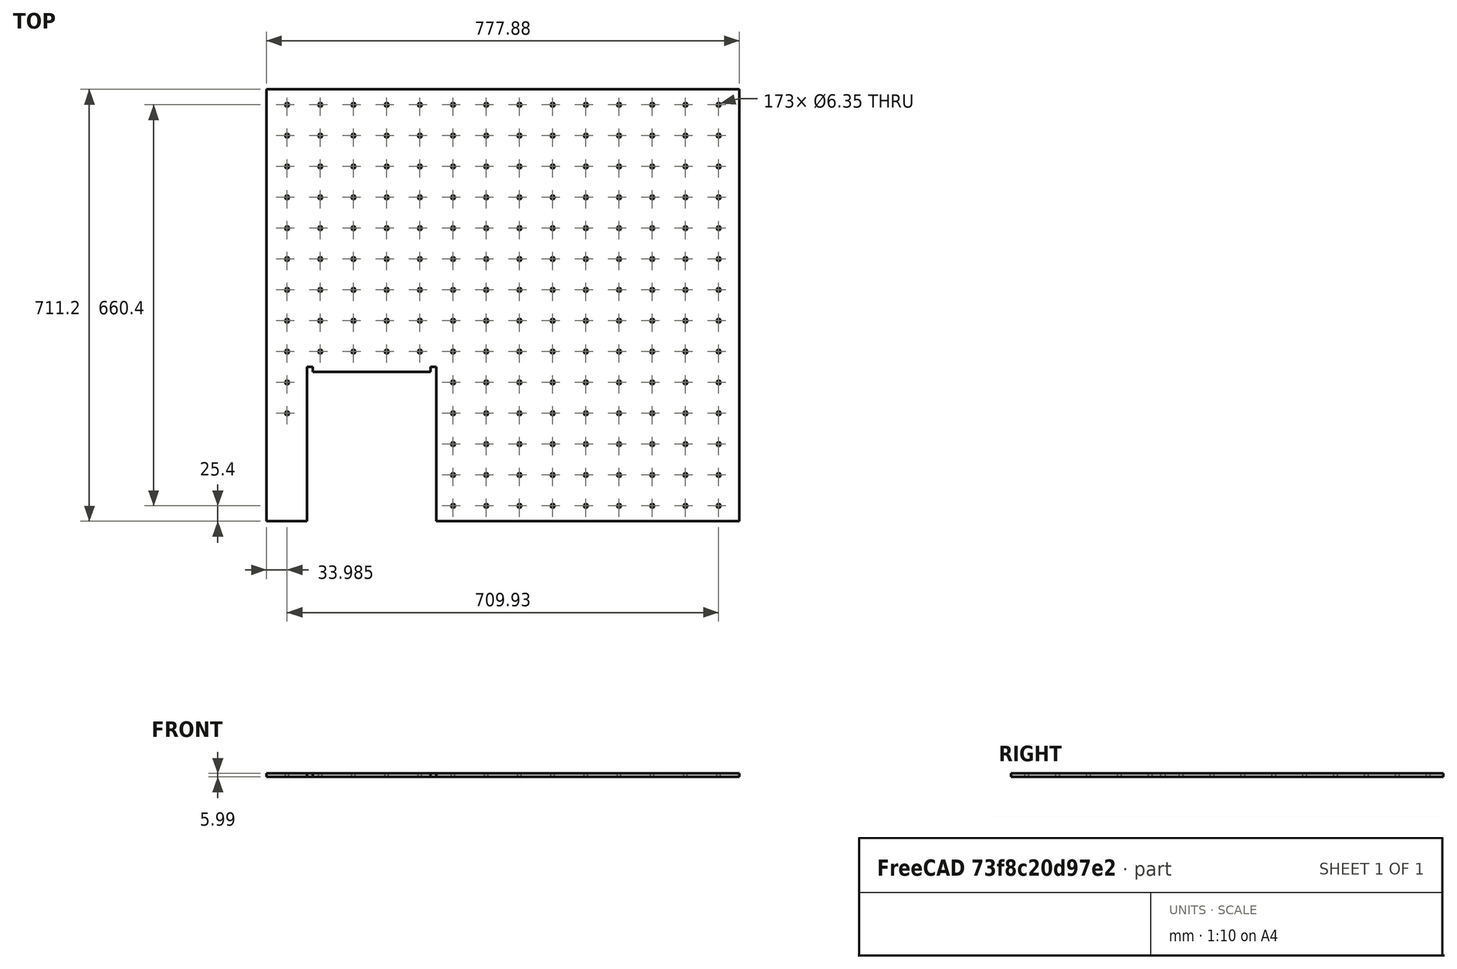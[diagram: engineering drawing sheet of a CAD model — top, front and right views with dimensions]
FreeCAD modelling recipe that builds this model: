
FCSTD DOCUMENT  (FreeCAD 0.19R24267 (Git))
Label: Inv1-P8
License: All rights reserved
LicenseURL: http://en.wikipedia.org/wiki/All_rights_reserved
objects: TechDraw::DrawViewDimension×15, TechDraw::DrawViewAnnotation×3, TechDraw::DrawProjGroupItem×2, TechDraw::DrawHatch×2, Sketcher::SketchObject×1, Part::Extrusion×1, TechDraw::DrawSVGTemplate×1, TechDraw::DrawProjGroup×1, TechDraw::DrawPage×1
note: 2 computed .brp shape members not serialized (recipe doc carries the construction recipe); baked Part::Feature solids carry a one-line shape summary decoded from their .brp

FEATURE [Sketcher::SketchObject] Sketch
  FullyConstrained = false
  sketch-geometry (352):
    g0: LineSegment StartX=0 StartY=0 StartZ=0 EndX=777.875 EndY=0 EndZ=0
    g1: LineSegment StartX=777.875 StartY=0 StartZ=0 EndX=777.875 EndY=-711.2 EndZ=0
    g2: LineSegment StartX=0 StartY=-711.2 StartZ=0 EndX=0 EndY=0 EndZ=0
    g3: LineSegment StartX=279.4 StartY=-711.2 StartZ=0 EndX=279.4 EndY=-457.2 EndZ=0
    g4: LineSegment StartX=66.675 StartY=-457.2 StartZ=0 EndX=66.675 EndY=-711.2 EndZ=0
    g5: LineSegment StartX=0 StartY=-711.2 StartZ=0 EndX=66.675 EndY=-711.2 EndZ=0
    g6: LineSegment StartX=279.4 StartY=-711.2 StartZ=0 EndX=777.875 EndY=-711.2 EndZ=0
    g7: LineSegment StartX=66.675 StartY=-457.2 StartZ=0 EndX=76.2 EndY=-457.2 EndZ=0
    g8: LineSegment StartX=76.2 StartY=-457.2 StartZ=0 EndX=76.2 EndY=-465.125 EndZ=0
    g9: LineSegment StartX=76.2 StartY=-465.125 StartZ=0 EndX=269.875 EndY=-465.125 EndZ=0
    g10: LineSegment StartX=269.875 StartY=-465.125 StartZ=0 EndX=269.875 EndY=-457.2 EndZ=0
    g11: LineSegment StartX=279.4 StartY=-457.2 StartZ=0 EndX=269.875 EndY=-457.2 EndZ=0
    g12: Circle CenterX=33.9852 CenterY=-25.4 CenterZ=0 NormalX=0 NormalY=0 NormalZ=1 AngleXU=0 Radius=3.175
    g13: Circle CenterX=88.5952 CenterY=-25.4 CenterZ=0 NormalX=0 NormalY=0 NormalZ=1 AngleXU=0 Radius=3.175
    g14: LineSegment StartX=33.9852 StartY=-25.4 StartZ=0 EndX=88.5952 EndY=-25.4 EndZ=0
    g15: Circle CenterX=143.205 CenterY=-25.4 CenterZ=0 NormalX=0 NormalY=0 NormalZ=1 AngleXU=0 Radius=3.175
    g16: LineSegment StartX=88.5952 StartY=-25.4 StartZ=0 EndX=143.205 EndY=-25.4 EndZ=0
    g17: Circle CenterX=197.815 CenterY=-25.4 CenterZ=0 NormalX=0 NormalY=0 NormalZ=1 AngleXU=0 Radius=3.175
    g18: LineSegment StartX=143.205 StartY=-25.4 StartZ=0 EndX=197.815 EndY=-25.4 EndZ=0
    g19: Circle CenterX=252.425 CenterY=-25.4 CenterZ=0 NormalX=0 NormalY=0 NormalZ=1 AngleXU=0 Radius=3.175
    g20: LineSegment StartX=197.815 StartY=-25.4 StartZ=0 EndX=252.425 EndY=-25.4 EndZ=0
    g21: Circle CenterX=307.035 CenterY=-25.4 CenterZ=0 NormalX=0 NormalY=0 NormalZ=1 AngleXU=0 Radius=3.175
    g22: LineSegment StartX=252.425 StartY=-25.4 StartZ=0 EndX=307.035 EndY=-25.4 EndZ=0
    g23: Circle CenterX=361.645 CenterY=-25.4 CenterZ=0 NormalX=0 NormalY=0 NormalZ=1 AngleXU=0 Radius=3.175
    g24: LineSegment StartX=307.035 StartY=-25.4 StartZ=0 EndX=361.645 EndY=-25.4 EndZ=0
    g25: Circle CenterX=416.255 CenterY=-25.4 CenterZ=0 NormalX=0 NormalY=0 NormalZ=1 AngleXU=0 Radius=3.175
    g26: LineSegment StartX=361.645 StartY=-25.4 StartZ=0 EndX=416.255 EndY=-25.4 EndZ=0
    g27: Circle CenterX=470.865 CenterY=-25.4 CenterZ=0 NormalX=0 NormalY=0 NormalZ=1 AngleXU=0 Radius=3.175
    g28: LineSegment StartX=416.255 StartY=-25.4 StartZ=0 EndX=470.865 EndY=-25.4 EndZ=0
    g29: Circle CenterX=525.475 CenterY=-25.4 CenterZ=0 NormalX=0 NormalY=0 NormalZ=1 AngleXU=0 Radius=3.175
    g30: LineSegment StartX=470.865 StartY=-25.4 StartZ=0 EndX=525.475 EndY=-25.4 EndZ=0
    g31: Circle CenterX=580.085 CenterY=-25.4 CenterZ=0 NormalX=0 NormalY=0 NormalZ=1 AngleXU=0 Radius=3.175
    g32: LineSegment StartX=525.475 StartY=-25.4 StartZ=0 EndX=580.085 EndY=-25.4 EndZ=0
    g33: Circle CenterX=634.695 CenterY=-25.4 CenterZ=0 NormalX=0 NormalY=0 NormalZ=1 AngleXU=0 Radius=3.175
    g34: LineSegment StartX=580.085 StartY=-25.4 StartZ=0 EndX=634.695 EndY=-25.4 EndZ=0
    g35: Circle CenterX=689.305 CenterY=-25.4 CenterZ=0 NormalX=0 NormalY=0 NormalZ=1 AngleXU=0 Radius=3.175
    g36: LineSegment StartX=634.695 StartY=-25.4 StartZ=0 EndX=689.305 EndY=-25.4 EndZ=0
    g37: Circle CenterX=743.915 CenterY=-25.4 CenterZ=0 NormalX=0 NormalY=0 NormalZ=1 AngleXU=0 Radius=3.175
    g38: LineSegment StartX=689.305 StartY=-25.4 StartZ=0 EndX=743.915 EndY=-25.4 EndZ=0
    g39: Circle CenterX=33.9852 CenterY=-76.2 CenterZ=0 NormalX=0 NormalY=0 NormalZ=1 AngleXU=0 Radius=3.175
    g40: LineSegment StartX=33.9852 StartY=-25.4 StartZ=0 EndX=33.9852 EndY=-76.2 EndZ=0
    g41: Circle CenterX=88.5952 CenterY=-76.2 CenterZ=0 NormalX=0 NormalY=0 NormalZ=1 AngleXU=0 Radius=3.175
    g42: LineSegment StartX=33.9852 StartY=-76.2 StartZ=0 EndX=88.5952 EndY=-76.2 EndZ=0
    g43: Circle CenterX=143.205 CenterY=-76.2 CenterZ=0 NormalX=0 NormalY=0 NormalZ=1 AngleXU=0 Radius=3.175
    g44: LineSegment StartX=88.5952 StartY=-76.2 StartZ=0 EndX=143.205 EndY=-76.2 EndZ=0
    g45: Circle CenterX=197.815 CenterY=-76.2 CenterZ=0 NormalX=0 NormalY=0 NormalZ=1 AngleXU=0 Radius=3.175
    g46: LineSegment StartX=143.205 StartY=-76.2 StartZ=0 EndX=197.815 EndY=-76.2 EndZ=0
    g47: Circle CenterX=252.425 CenterY=-76.2 CenterZ=0 NormalX=0 NormalY=0 NormalZ=1 AngleXU=0 Radius=3.175
    g48: LineSegment StartX=197.815 StartY=-76.2 StartZ=0 EndX=252.425 EndY=-76.2 EndZ=0
    g49: Circle CenterX=307.035 CenterY=-76.2 CenterZ=0 NormalX=0 NormalY=0 NormalZ=1 AngleXU=0 Radius=3.175
    g50: LineSegment StartX=252.425 StartY=-76.2 StartZ=0 EndX=307.035 EndY=-76.2 EndZ=0
    g51: Circle CenterX=361.645 CenterY=-76.2 CenterZ=0 NormalX=0 NormalY=0 NormalZ=1 AngleXU=0 Radius=3.175
    g52: LineSegment StartX=307.035 StartY=-76.2 StartZ=0 EndX=361.645 EndY=-76.2 EndZ=0
    g53: Circle CenterX=416.255 CenterY=-76.2 CenterZ=0 NormalX=0 NormalY=0 NormalZ=1 AngleXU=0 Radius=3.175
    g54: LineSegment StartX=361.645 StartY=-76.2 StartZ=0 EndX=416.255 EndY=-76.2 EndZ=0
    g55: Circle CenterX=470.865 CenterY=-76.2 CenterZ=0 NormalX=0 NormalY=0 NormalZ=1 AngleXU=0 Radius=3.175
    g56: LineSegment StartX=416.255 StartY=-76.2 StartZ=0 EndX=470.865 EndY=-76.2 EndZ=0
    g57: Circle CenterX=525.475 CenterY=-76.2 CenterZ=0 NormalX=0 NormalY=0 NormalZ=1 AngleXU=0 Radius=3.175
    g58: LineSegment StartX=470.865 StartY=-76.2 StartZ=0 EndX=525.475 EndY=-76.2 EndZ=0
    g59: Circle CenterX=580.085 CenterY=-76.2 CenterZ=0 NormalX=0 NormalY=0 NormalZ=1 AngleXU=0 Radius=3.175
    g60: LineSegment StartX=525.475 StartY=-76.2 StartZ=0 EndX=580.085 EndY=-76.2 EndZ=0
    g61: Circle CenterX=634.695 CenterY=-76.2 CenterZ=0 NormalX=0 NormalY=0 NormalZ=1 AngleXU=0 Radius=3.175
    g62: LineSegment StartX=580.085 StartY=-76.2 StartZ=0 EndX=634.695 EndY=-76.2 EndZ=0
    g63: Circle CenterX=689.305 CenterY=-76.2 CenterZ=0 NormalX=0 NormalY=0 NormalZ=1 AngleXU=0 Radius=3.175
    g64: LineSegment StartX=634.695 StartY=-76.2 StartZ=0 EndX=689.305 EndY=-76.2 EndZ=0
    g65: Circle CenterX=743.915 CenterY=-76.2 CenterZ=0 NormalX=0 NormalY=0 NormalZ=1 AngleXU=0 Radius=3.175
    g66: LineSegment StartX=689.305 StartY=-76.2 StartZ=0 EndX=743.915 EndY=-76.2 EndZ=0
    g67: Circle CenterX=33.9852 CenterY=-127 CenterZ=0 NormalX=0 NormalY=0 NormalZ=1 AngleXU=0 Radius=3.175
    g68: LineSegment StartX=33.9852 StartY=-76.2 StartZ=0 EndX=33.9852 EndY=-127 EndZ=0
    g69: Circle CenterX=88.5952 CenterY=-127 CenterZ=0 NormalX=0 NormalY=0 NormalZ=1 AngleXU=0 Radius=3.175
    g70: LineSegment StartX=33.9852 StartY=-127 StartZ=0 EndX=88.5952 EndY=-127 EndZ=0
    g71: Circle CenterX=143.205 CenterY=-127 CenterZ=0 NormalX=0 NormalY=0 NormalZ=1 AngleXU=0 Radius=3.175
    g72: LineSegment StartX=88.5952 StartY=-127 StartZ=0 EndX=143.205 EndY=-127 EndZ=0
    g73: Circle CenterX=197.815 CenterY=-127 CenterZ=0 NormalX=0 NormalY=0 NormalZ=1 AngleXU=0 Radius=3.175
    g74: LineSegment StartX=143.205 StartY=-127 StartZ=0 EndX=197.815 EndY=-127 EndZ=0
    g75: Circle CenterX=252.425 CenterY=-127 CenterZ=0 NormalX=0 NormalY=0 NormalZ=1 AngleXU=0 Radius=3.175
    g76: LineSegment StartX=197.815 StartY=-127 StartZ=0 EndX=252.425 EndY=-127 EndZ=0
    g77: Circle CenterX=307.035 CenterY=-127 CenterZ=0 NormalX=0 NormalY=0 NormalZ=1 AngleXU=0 Radius=3.175
    g78: LineSegment StartX=252.425 StartY=-127 StartZ=0 EndX=307.035 EndY=-127 EndZ=0
    g79: Circle CenterX=361.645 CenterY=-127 CenterZ=0 NormalX=0 NormalY=0 NormalZ=1 AngleXU=0 Radius=3.175
    g80: LineSegment StartX=307.035 StartY=-127 StartZ=0 EndX=361.645 EndY=-127 EndZ=0
    g81: Circle CenterX=416.255 CenterY=-127 CenterZ=0 NormalX=0 NormalY=0 NormalZ=1 AngleXU=0 Radius=3.175
    g82: LineSegment StartX=361.645 StartY=-127 StartZ=0 EndX=416.255 EndY=-127 EndZ=0
    g83: Circle CenterX=470.865 CenterY=-127 CenterZ=0 NormalX=0 NormalY=0 NormalZ=1 AngleXU=0 Radius=3.175
    g84: LineSegment StartX=416.255 StartY=-127 StartZ=0 EndX=470.865 EndY=-127 EndZ=0
    g85: Circle CenterX=525.475 CenterY=-127 CenterZ=0 NormalX=0 NormalY=0 NormalZ=1 AngleXU=0 Radius=3.175
    g86: LineSegment StartX=470.865 StartY=-127 StartZ=0 EndX=525.475 EndY=-127 EndZ=0
    g87: Circle CenterX=580.085 CenterY=-127 CenterZ=0 NormalX=0 NormalY=0 NormalZ=1 AngleXU=0 Radius=3.175
    g88: LineSegment StartX=525.475 StartY=-127 StartZ=0 EndX=580.085 EndY=-127 EndZ=0
    g89: Circle CenterX=634.695 CenterY=-127 CenterZ=0 NormalX=0 NormalY=0 NormalZ=1 AngleXU=0 Radius=3.175
    g90: LineSegment StartX=580.085 StartY=-127 StartZ=0 EndX=634.695 EndY=-127 EndZ=0
    g91: Circle CenterX=689.305 CenterY=-127 CenterZ=0 NormalX=0 NormalY=0 NormalZ=1 AngleXU=0 Radius=3.175
    g92: LineSegment StartX=634.695 StartY=-127 StartZ=0 EndX=689.305 EndY=-127 EndZ=0
    g93: Circle CenterX=743.915 CenterY=-127 CenterZ=0 NormalX=0 NormalY=0 NormalZ=1 AngleXU=0 Radius=3.175
    g94: LineSegment StartX=689.305 StartY=-127 StartZ=0 EndX=743.915 EndY=-127 EndZ=0
    g95: Circle CenterX=33.9852 CenterY=-177.8 CenterZ=0 NormalX=0 NormalY=0 NormalZ=1 AngleXU=0 Radius=3.175
    g96: LineSegment StartX=33.9852 StartY=-127 StartZ=0 EndX=33.9852 EndY=-177.8 EndZ=0
    g97: Circle CenterX=88.5952 CenterY=-177.8 CenterZ=0 NormalX=0 NormalY=0 NormalZ=1 AngleXU=0 Radius=3.175
    g98: LineSegment StartX=33.9852 StartY=-177.8 StartZ=0 EndX=88.5952 EndY=-177.8 EndZ=0
    g99: Circle CenterX=143.205 CenterY=-177.8 CenterZ=0 NormalX=0 NormalY=0 NormalZ=1 AngleXU=0 Radius=3.175
    g100: LineSegment StartX=88.5952 StartY=-177.8 StartZ=0 EndX=143.205 EndY=-177.8 EndZ=0
    g101: Circle CenterX=197.815 CenterY=-177.8 CenterZ=0 NormalX=0 NormalY=0 NormalZ=1 AngleXU=0 Radius=3.175
    g102: LineSegment StartX=143.205 StartY=-177.8 StartZ=0 EndX=197.815 EndY=-177.8 EndZ=0
    g103: Circle CenterX=252.425 CenterY=-177.8 CenterZ=0 NormalX=0 NormalY=0 NormalZ=1 AngleXU=0 Radius=3.175
    g104: LineSegment StartX=197.815 StartY=-177.8 StartZ=0 EndX=252.425 EndY=-177.8 EndZ=0
    g105: Circle CenterX=307.035 CenterY=-177.8 CenterZ=0 NormalX=0 NormalY=0 NormalZ=1 AngleXU=0 Radius=3.175
    g106: LineSegment StartX=252.425 StartY=-177.8 StartZ=0 EndX=307.035 EndY=-177.8 EndZ=0
    g107: Circle CenterX=361.645 CenterY=-177.8 CenterZ=0 NormalX=0 NormalY=0 NormalZ=1 AngleXU=0 Radius=3.175
    g108: LineSegment StartX=307.035 StartY=-177.8 StartZ=0 EndX=361.645 EndY=-177.8 EndZ=0
    g109: Circle CenterX=416.255 CenterY=-177.8 CenterZ=0 NormalX=0 NormalY=0 NormalZ=1 AngleXU=0 Radius=3.175
    g110: LineSegment StartX=361.645 StartY=-177.8 StartZ=0 EndX=416.255 EndY=-177.8 EndZ=0
    g111: Circle CenterX=470.865 CenterY=-177.8 CenterZ=0 NormalX=0 NormalY=0 NormalZ=1 AngleXU=0 Radius=3.175
    g112: LineSegment StartX=416.255 StartY=-177.8 StartZ=0 EndX=470.865 EndY=-177.8 EndZ=0
    g113: Circle CenterX=525.475 CenterY=-177.8 CenterZ=0 NormalX=0 NormalY=0 NormalZ=1 AngleXU=0 Radius=3.175
    g114: LineSegment StartX=470.865 StartY=-177.8 StartZ=0 EndX=525.475 EndY=-177.8 EndZ=0
    g115: Circle CenterX=580.085 CenterY=-177.8 CenterZ=0 NormalX=0 NormalY=0 NormalZ=1 AngleXU=0 Radius=3.175
    g116: LineSegment StartX=525.475 StartY=-177.8 StartZ=0 EndX=580.085 EndY=-177.8 EndZ=0
    g117: Circle CenterX=634.695 CenterY=-177.8 CenterZ=0 NormalX=0 NormalY=0 NormalZ=1 AngleXU=0 Radius=3.175
    g118: LineSegment StartX=580.085 StartY=-177.8 StartZ=0 EndX=634.695 EndY=-177.8 EndZ=0
    g119: Circle CenterX=689.305 CenterY=-177.8 CenterZ=0 NormalX=0 NormalY=0 NormalZ=1 AngleXU=0 Radius=3.175
    g120: LineSegment StartX=634.695 StartY=-177.8 StartZ=0 EndX=689.305 EndY=-177.8 EndZ=0
    g121: Circle CenterX=743.915 CenterY=-177.8 CenterZ=0 NormalX=0 NormalY=0 NormalZ=1 AngleXU=0 Radius=3.175
    g122: LineSegment StartX=689.305 StartY=-177.8 StartZ=0 EndX=743.915 EndY=-177.8 EndZ=0
    g123: Circle CenterX=33.9852 CenterY=-228.6 CenterZ=0 NormalX=0 NormalY=0 NormalZ=1 AngleXU=0 Radius=3.175
    g124: LineSegment StartX=33.9852 StartY=-177.8 StartZ=0 EndX=33.9852 EndY=-228.6 EndZ=0
    g125: Circle CenterX=88.5952 CenterY=-228.6 CenterZ=0 NormalX=0 NormalY=0 NormalZ=1 AngleXU=0 Radius=3.175
    g126: LineSegment StartX=33.9852 StartY=-228.6 StartZ=0 EndX=88.5952 EndY=-228.6 EndZ=0
    g127: Circle CenterX=143.205 CenterY=-228.6 CenterZ=0 NormalX=0 NormalY=0 NormalZ=1 AngleXU=0 Radius=3.175
    g128: LineSegment StartX=88.5952 StartY=-228.6 StartZ=0 EndX=143.205 EndY=-228.6 EndZ=0
    g129: Circle CenterX=197.815 CenterY=-228.6 CenterZ=0 NormalX=0 NormalY=0 NormalZ=1 AngleXU=0 Radius=3.175
    g130: LineSegment StartX=143.205 StartY=-228.6 StartZ=0 EndX=197.815 EndY=-228.6 EndZ=0
    g131: Circle CenterX=252.425 CenterY=-228.6 CenterZ=0 NormalX=0 NormalY=0 NormalZ=1 AngleXU=0 Radius=3.175
    g132: LineSegment StartX=197.815 StartY=-228.6 StartZ=0 EndX=252.425 EndY=-228.6 EndZ=0
    g133: Circle CenterX=307.035 CenterY=-228.6 CenterZ=0 NormalX=0 NormalY=0 NormalZ=1 AngleXU=0 Radius=3.175
    g134: LineSegment StartX=252.425 StartY=-228.6 StartZ=0 EndX=307.035 EndY=-228.6 EndZ=0
    g135: Circle CenterX=361.645 CenterY=-228.6 CenterZ=0 NormalX=0 NormalY=0 NormalZ=1 AngleXU=0 Radius=3.175
    g136: LineSegment StartX=307.035 StartY=-228.6 StartZ=0 EndX=361.645 EndY=-228.6 EndZ=0
    g137: Circle CenterX=416.255 CenterY=-228.6 CenterZ=0 NormalX=0 NormalY=0 NormalZ=1 AngleXU=0 Radius=3.175
    g138: LineSegment StartX=361.645 StartY=-228.6 StartZ=0 EndX=416.255 EndY=-228.6 EndZ=0
    g139: Circle CenterX=470.865 CenterY=-228.6 CenterZ=0 NormalX=0 NormalY=0 NormalZ=1 AngleXU=0 Radius=3.175
    g140: LineSegment StartX=416.255 StartY=-228.6 StartZ=0 EndX=470.865 EndY=-228.6 EndZ=0
    g141: Circle CenterX=525.475 CenterY=-228.6 CenterZ=0 NormalX=0 NormalY=0 NormalZ=1 AngleXU=0 Radius=3.175
    g142: LineSegment StartX=470.865 StartY=-228.6 StartZ=0 EndX=525.475 EndY=-228.6 EndZ=0
    g143: Circle CenterX=580.085 CenterY=-228.6 CenterZ=0 NormalX=0 NormalY=0 NormalZ=1 AngleXU=0 Radius=3.175
    g144: LineSegment StartX=525.475 StartY=-228.6 StartZ=0 EndX=580.085 EndY=-228.6 EndZ=0
    g145: Circle CenterX=634.695 CenterY=-228.6 CenterZ=0 NormalX=0 NormalY=0 NormalZ=1 AngleXU=0 Radius=3.175
    g146: LineSegment StartX=580.085 StartY=-228.6 StartZ=0 EndX=634.695 EndY=-228.6 EndZ=0
    g147: Circle CenterX=689.305 CenterY=-228.6 CenterZ=0 NormalX=0 NormalY=0 NormalZ=1 AngleXU=0 Radius=3.175
    g148: LineSegment StartX=634.695 StartY=-228.6 StartZ=0 EndX=689.305 EndY=-228.6 EndZ=0
    g149: Circle CenterX=743.915 CenterY=-228.6 CenterZ=0 NormalX=0 NormalY=0 NormalZ=1 AngleXU=0 Radius=3.175
    g150: LineSegment StartX=689.305 StartY=-228.6 StartZ=0 EndX=743.915 EndY=-228.6 EndZ=0
    g151: Circle CenterX=33.9852 CenterY=-279.4 CenterZ=0 NormalX=0 NormalY=0 NormalZ=1 AngleXU=0 Radius=3.175
    g152: LineSegment StartX=33.9852 StartY=-228.6 StartZ=0 EndX=33.9852 EndY=-279.4 EndZ=0
    g153: Circle CenterX=88.5952 CenterY=-279.4 CenterZ=0 NormalX=0 NormalY=0 NormalZ=1 AngleXU=0 Radius=3.175
    g154: LineSegment StartX=33.9852 StartY=-279.4 StartZ=0 EndX=88.5952 EndY=-279.4 EndZ=0
    g155: Circle CenterX=143.205 CenterY=-279.4 CenterZ=0 NormalX=0 NormalY=0 NormalZ=1 AngleXU=0 Radius=3.175
    g156: LineSegment StartX=88.5952 StartY=-279.4 StartZ=0 EndX=143.205 EndY=-279.4 EndZ=0
    g157: Circle CenterX=197.815 CenterY=-279.4 CenterZ=0 NormalX=0 NormalY=0 NormalZ=1 AngleXU=0 Radius=3.175
    g158: LineSegment StartX=143.205 StartY=-279.4 StartZ=0 EndX=197.815 EndY=-279.4 EndZ=0
    g159: Circle CenterX=252.425 CenterY=-279.4 CenterZ=0 NormalX=0 NormalY=0 NormalZ=1 AngleXU=0 Radius=3.175
    g160: LineSegment StartX=197.815 StartY=-279.4 StartZ=0 EndX=252.425 EndY=-279.4 EndZ=0
    g161: Circle CenterX=307.035 CenterY=-279.4 CenterZ=0 NormalX=0 NormalY=0 NormalZ=1 AngleXU=0 Radius=3.175
    g162: LineSegment StartX=252.425 StartY=-279.4 StartZ=0 EndX=307.035 EndY=-279.4 EndZ=0
    g163: Circle CenterX=361.645 CenterY=-279.4 CenterZ=0 NormalX=0 NormalY=0 NormalZ=1 AngleXU=0 Radius=3.175
    g164: LineSegment StartX=307.035 StartY=-279.4 StartZ=0 EndX=361.645 EndY=-279.4 EndZ=0
    g165: Circle CenterX=416.255 CenterY=-279.4 CenterZ=0 NormalX=0 NormalY=0 NormalZ=1 AngleXU=0 Radius=3.175
    g166: LineSegment StartX=361.645 StartY=-279.4 StartZ=0 EndX=416.255 EndY=-279.4 EndZ=0
    g167: Circle CenterX=470.865 CenterY=-279.4 CenterZ=0 NormalX=0 NormalY=0 NormalZ=1 AngleXU=0 Radius=3.175
    g168: LineSegment StartX=416.255 StartY=-279.4 StartZ=0 EndX=470.865 EndY=-279.4 EndZ=0
    g169: Circle CenterX=525.475 CenterY=-279.4 CenterZ=0 NormalX=0 NormalY=0 NormalZ=1 AngleXU=0 Radius=3.175
    g170: LineSegment StartX=470.865 StartY=-279.4 StartZ=0 EndX=525.475 EndY=-279.4 EndZ=0
    g171: Circle CenterX=580.085 CenterY=-279.4 CenterZ=0 NormalX=0 NormalY=0 NormalZ=1 AngleXU=0 Radius=3.175
    g172: LineSegment StartX=525.475 StartY=-279.4 StartZ=0 EndX=580.085 EndY=-279.4 EndZ=0
    g173: Circle CenterX=634.695 CenterY=-279.4 CenterZ=0 NormalX=0 NormalY=0 NormalZ=1 AngleXU=0 Radius=3.175
    g174: LineSegment StartX=580.085 StartY=-279.4 StartZ=0 EndX=634.695 EndY=-279.4 EndZ=0
    g175: Circle CenterX=689.305 CenterY=-279.4 CenterZ=0 NormalX=0 NormalY=0 NormalZ=1 AngleXU=0 Radius=3.175
    g176: LineSegment StartX=634.695 StartY=-279.4 StartZ=0 EndX=689.305 EndY=-279.4 EndZ=0
    g177: Circle CenterX=743.915 CenterY=-279.4 CenterZ=0 NormalX=0 NormalY=0 NormalZ=1 AngleXU=0 Radius=3.175
    g178: LineSegment StartX=689.305 StartY=-279.4 StartZ=0 EndX=743.915 EndY=-279.4 EndZ=0
    g179: Circle CenterX=33.9852 CenterY=-330.2 CenterZ=0 NormalX=0 NormalY=0 NormalZ=1 AngleXU=0 Radius=3.175
    g180: LineSegment StartX=33.9852 StartY=-279.4 StartZ=0 EndX=33.9852 EndY=-330.2 EndZ=0
    g181: Circle CenterX=88.5952 CenterY=-330.2 CenterZ=0 NormalX=0 NormalY=0 NormalZ=1 AngleXU=0 Radius=3.175
    g182: LineSegment StartX=33.9852 StartY=-330.2 StartZ=0 EndX=88.5952 EndY=-330.2 EndZ=0
    g183: Circle CenterX=143.205 CenterY=-330.2 CenterZ=0 NormalX=0 NormalY=0 NormalZ=1 AngleXU=0 Radius=3.175
    g184: LineSegment StartX=88.5952 StartY=-330.2 StartZ=0 EndX=143.205 EndY=-330.2 EndZ=0
    g185: Circle CenterX=197.815 CenterY=-330.2 CenterZ=0 NormalX=0 NormalY=0 NormalZ=1 AngleXU=0 Radius=3.175
    g186: LineSegment StartX=143.205 StartY=-330.2 StartZ=0 EndX=197.815 EndY=-330.2 EndZ=0
    g187: Circle CenterX=252.425 CenterY=-330.2 CenterZ=0 NormalX=0 NormalY=0 NormalZ=1 AngleXU=0 Radius=3.175
    g188: LineSegment StartX=197.815 StartY=-330.2 StartZ=0 EndX=252.425 EndY=-330.2 EndZ=0
    g189: Circle CenterX=307.035 CenterY=-330.2 CenterZ=0 NormalX=0 NormalY=0 NormalZ=1 AngleXU=0 Radius=3.175
    g190: LineSegment StartX=252.425 StartY=-330.2 StartZ=0 EndX=307.035 EndY=-330.2 EndZ=0
    g191: Circle CenterX=361.645 CenterY=-330.2 CenterZ=0 NormalX=0 NormalY=0 NormalZ=1 AngleXU=0 Radius=3.175
    g192: LineSegment StartX=307.035 StartY=-330.2 StartZ=0 EndX=361.645 EndY=-330.2 EndZ=0
    g193: Circle CenterX=416.255 CenterY=-330.2 CenterZ=0 NormalX=0 NormalY=0 NormalZ=1 AngleXU=0 Radius=3.175
    g194: LineSegment StartX=361.645 StartY=-330.2 StartZ=0 EndX=416.255 EndY=-330.2 EndZ=0
    g195: Circle CenterX=470.865 CenterY=-330.2 CenterZ=0 NormalX=0 NormalY=0 NormalZ=1 AngleXU=0 Radius=3.175
    g196: LineSegment StartX=416.255 StartY=-330.2 StartZ=0 EndX=470.865 EndY=-330.2 EndZ=0
    g197: Circle CenterX=525.475 CenterY=-330.2 CenterZ=0 NormalX=0 NormalY=0 NormalZ=1 AngleXU=0 Radius=3.175
    g198: LineSegment StartX=470.865 StartY=-330.2 StartZ=0 EndX=525.475 EndY=-330.2 EndZ=0
    g199: Circle CenterX=580.085 CenterY=-330.2 CenterZ=0 NormalX=0 NormalY=0 NormalZ=1 AngleXU=0 Radius=3.175
    g200: LineSegment StartX=525.475 StartY=-330.2 StartZ=0 EndX=580.085 EndY=-330.2 EndZ=0
    g201: Circle CenterX=634.695 CenterY=-330.2 CenterZ=0 NormalX=0 NormalY=0 NormalZ=1 AngleXU=0 Radius=3.175
    g202: LineSegment StartX=580.085 StartY=-330.2 StartZ=0 EndX=634.695 EndY=-330.2 EndZ=0
    g203: Circle CenterX=689.305 CenterY=-330.2 CenterZ=0 NormalX=0 NormalY=0 NormalZ=1 AngleXU=0 Radius=3.175
    g204: LineSegment StartX=634.695 StartY=-330.2 StartZ=0 EndX=689.305 EndY=-330.2 EndZ=0
    g205: Circle CenterX=743.915 CenterY=-330.2 CenterZ=0 NormalX=0 NormalY=0 NormalZ=1 AngleXU=0 Radius=3.175
    g206: LineSegment StartX=689.305 StartY=-330.2 StartZ=0 EndX=743.915 EndY=-330.2 EndZ=0
    g207: Circle CenterX=33.9852 CenterY=-381 CenterZ=0 NormalX=0 NormalY=0 NormalZ=1 AngleXU=0 Radius=3.175
    g208: LineSegment StartX=33.9852 StartY=-330.2 StartZ=0 EndX=33.9852 EndY=-381 EndZ=0
    g209: Circle CenterX=88.5952 CenterY=-381 CenterZ=0 NormalX=0 NormalY=0 NormalZ=1 AngleXU=0 Radius=3.175
    g210: LineSegment StartX=33.9852 StartY=-381 StartZ=0 EndX=88.5952 EndY=-381 EndZ=0
    g211: Circle CenterX=143.205 CenterY=-381 CenterZ=0 NormalX=0 NormalY=0 NormalZ=1 AngleXU=0 Radius=3.175
    g212: LineSegment StartX=88.5952 StartY=-381 StartZ=0 EndX=143.205 EndY=-381 EndZ=0
    g213: Circle CenterX=197.815 CenterY=-381 CenterZ=0 NormalX=0 NormalY=0 NormalZ=1 AngleXU=0 Radius=3.175
    g214: LineSegment StartX=143.205 StartY=-381 StartZ=0 EndX=197.815 EndY=-381 EndZ=0
    g215: Circle CenterX=252.425 CenterY=-381 CenterZ=0 NormalX=0 NormalY=0 NormalZ=1 AngleXU=0 Radius=3.175
    g216: LineSegment StartX=197.815 StartY=-381 StartZ=0 EndX=252.425 EndY=-381 EndZ=0
    g217: Circle CenterX=307.035 CenterY=-381 CenterZ=0 NormalX=0 NormalY=0 NormalZ=1 AngleXU=0 Radius=3.175
    g218: LineSegment StartX=252.425 StartY=-381 StartZ=0 EndX=307.035 EndY=-381 EndZ=0
    g219: Circle CenterX=361.645 CenterY=-381 CenterZ=0 NormalX=0 NormalY=0 NormalZ=1 AngleXU=0 Radius=3.175
    g220: LineSegment StartX=307.035 StartY=-381 StartZ=0 EndX=361.645 EndY=-381 EndZ=0
    g221: Circle CenterX=416.255 CenterY=-381 CenterZ=0 NormalX=0 NormalY=0 NormalZ=1 AngleXU=0 Radius=3.175
    g222: LineSegment StartX=361.645 StartY=-381 StartZ=0 EndX=416.255 EndY=-381 EndZ=0
    g223: Circle CenterX=470.865 CenterY=-381 CenterZ=0 NormalX=0 NormalY=0 NormalZ=1 AngleXU=0 Radius=3.175
    g224: LineSegment StartX=416.255 StartY=-381 StartZ=0 EndX=470.865 EndY=-381 EndZ=0
    g225: Circle CenterX=525.475 CenterY=-381 CenterZ=0 NormalX=0 NormalY=0 NormalZ=1 AngleXU=0 Radius=3.175
    g226: LineSegment StartX=470.865 StartY=-381 StartZ=0 EndX=525.475 EndY=-381 EndZ=0
    g227: Circle CenterX=580.085 CenterY=-381 CenterZ=0 NormalX=0 NormalY=0 NormalZ=1 AngleXU=0 Radius=3.175
    g228: LineSegment StartX=525.475 StartY=-381 StartZ=0 EndX=580.085 EndY=-381 EndZ=0
    g229: Circle CenterX=634.695 CenterY=-381 CenterZ=0 NormalX=0 NormalY=0 NormalZ=1 AngleXU=0 Radius=3.175
    g230: LineSegment StartX=580.085 StartY=-381 StartZ=0 EndX=634.695 EndY=-381 EndZ=0
    g231: Circle CenterX=689.305 CenterY=-381 CenterZ=0 NormalX=0 NormalY=0 NormalZ=1 AngleXU=0 Radius=3.175
    g232: LineSegment StartX=634.695 StartY=-381 StartZ=0 EndX=689.305 EndY=-381 EndZ=0
    g233: Circle CenterX=743.915 CenterY=-381 CenterZ=0 NormalX=0 NormalY=0 NormalZ=1 AngleXU=0 Radius=3.175
    g234: LineSegment StartX=689.305 StartY=-381 StartZ=0 EndX=743.915 EndY=-381 EndZ=0
    g235: Circle CenterX=33.9852 CenterY=-431.8 CenterZ=0 NormalX=0 NormalY=0 NormalZ=1 AngleXU=0 Radius=3.175
    g236: LineSegment StartX=33.9852 StartY=-381 StartZ=0 EndX=33.9852 EndY=-431.8 EndZ=0
    g237: Circle CenterX=88.5952 CenterY=-431.8 CenterZ=0 NormalX=0 NormalY=0 NormalZ=1 AngleXU=0 Radius=3.175
    g238: LineSegment StartX=33.9852 StartY=-431.8 StartZ=0 EndX=88.5952 EndY=-431.8 EndZ=0
    g239: Circle CenterX=143.205 CenterY=-431.8 CenterZ=0 NormalX=0 NormalY=0 NormalZ=1 AngleXU=0 Radius=3.175
    g240: LineSegment StartX=88.5952 StartY=-431.8 StartZ=0 EndX=143.205 EndY=-431.8 EndZ=0
    g241: Circle CenterX=197.815 CenterY=-431.8 CenterZ=0 NormalX=0 NormalY=0 NormalZ=1 AngleXU=0 Radius=3.175
    g242: LineSegment StartX=143.205 StartY=-431.8 StartZ=0 EndX=197.815 EndY=-431.8 EndZ=0
    g243: Circle CenterX=252.425 CenterY=-431.8 CenterZ=0 NormalX=0 NormalY=0 NormalZ=1 AngleXU=0 Radius=3.175
    g244: LineSegment StartX=197.815 StartY=-431.8 StartZ=0 EndX=252.425 EndY=-431.8 EndZ=0
    g245: Circle CenterX=307.035 CenterY=-431.8 CenterZ=0 NormalX=0 NormalY=0 NormalZ=1 AngleXU=0 Radius=3.175
    g246: LineSegment StartX=252.425 StartY=-431.8 StartZ=0 EndX=307.035 EndY=-431.8 EndZ=0
    g247: Circle CenterX=361.645 CenterY=-431.8 CenterZ=0 NormalX=0 NormalY=0 NormalZ=1 AngleXU=0 Radius=3.175
    g248: LineSegment StartX=307.035 StartY=-431.8 StartZ=0 EndX=361.645 EndY=-431.8 EndZ=0
    g249: Circle CenterX=416.255 CenterY=-431.8 CenterZ=0 NormalX=0 NormalY=0 NormalZ=1 AngleXU=0 Radius=3.175
    g250: LineSegment StartX=361.645 StartY=-431.8 StartZ=0 EndX=416.255 EndY=-431.8 EndZ=0
    g251: Circle CenterX=470.865 CenterY=-431.8 CenterZ=0 NormalX=0 NormalY=0 NormalZ=1 AngleXU=0 Radius=3.175
    g252: LineSegment StartX=416.255 StartY=-431.8 StartZ=0 EndX=470.865 EndY=-431.8 EndZ=0
    g253: Circle CenterX=525.475 CenterY=-431.8 CenterZ=0 NormalX=0 NormalY=0 NormalZ=1 AngleXU=0 Radius=3.175
    g254: LineSegment StartX=470.865 StartY=-431.8 StartZ=0 EndX=525.475 EndY=-431.8 EndZ=0
    g255: Circle CenterX=580.085 CenterY=-431.8 CenterZ=0 NormalX=0 NormalY=0 NormalZ=1 AngleXU=0 Radius=3.175
    g256: LineSegment StartX=525.475 StartY=-431.8 StartZ=0 EndX=580.085 EndY=-431.8 EndZ=0
    g257: Circle CenterX=634.695 CenterY=-431.8 CenterZ=0 NormalX=0 NormalY=0 NormalZ=1 AngleXU=0 Radius=3.175
    g258: LineSegment StartX=580.085 StartY=-431.8 StartZ=0 EndX=634.695 EndY=-431.8 EndZ=0
    g259: Circle CenterX=689.305 CenterY=-431.8 CenterZ=0 NormalX=0 NormalY=0 NormalZ=1 AngleXU=0 Radius=3.175
    g260: LineSegment StartX=634.695 StartY=-431.8 StartZ=0 EndX=689.305 EndY=-431.8 EndZ=0
    g261: Circle CenterX=743.915 CenterY=-431.8 CenterZ=0 NormalX=0 NormalY=0 NormalZ=1 AngleXU=0 Radius=3.175
    g262: LineSegment StartX=689.305 StartY=-431.8 StartZ=0 EndX=743.915 EndY=-431.8 EndZ=0
    g263: Circle CenterX=33.9852 CenterY=-482.6 CenterZ=0 NormalX=0 NormalY=0 NormalZ=1 AngleXU=0 Radius=3.175
    g264: LineSegment StartX=33.9852 StartY=-431.8 StartZ=0 EndX=33.9852 EndY=-482.6 EndZ=0
    g265: Circle CenterX=307.035 CenterY=-482.6 CenterZ=0 NormalX=0 NormalY=0 NormalZ=1 AngleXU=0 Radius=3.175
    g266: Circle CenterX=361.645 CenterY=-482.6 CenterZ=0 NormalX=0 NormalY=0 NormalZ=1 AngleXU=0 Radius=3.175
    g267: LineSegment StartX=307.035 StartY=-482.6 StartZ=0 EndX=361.645 EndY=-482.6 EndZ=0
    g268: Circle CenterX=416.255 CenterY=-482.6 CenterZ=0 NormalX=0 NormalY=0 NormalZ=1 AngleXU=0 Radius=3.175
    g269: LineSegment StartX=361.645 StartY=-482.6 StartZ=0 EndX=416.255 EndY=-482.6 EndZ=0
    g270: Circle CenterX=470.865 CenterY=-482.6 CenterZ=0 NormalX=0 NormalY=0 NormalZ=1 AngleXU=0 Radius=3.175
    g271: LineSegment StartX=416.255 StartY=-482.6 StartZ=0 EndX=470.865 EndY=-482.6 EndZ=0
    g272: Circle CenterX=525.475 CenterY=-482.6 CenterZ=0 NormalX=0 NormalY=0 NormalZ=1 AngleXU=0 Radius=3.175
    g273: LineSegment StartX=470.865 StartY=-482.6 StartZ=0 EndX=525.475 EndY=-482.6 EndZ=0
    g274: Circle CenterX=580.085 CenterY=-482.6 CenterZ=0 NormalX=0 NormalY=0 NormalZ=1 AngleXU=0 Radius=3.175
    g275: LineSegment StartX=525.475 StartY=-482.6 StartZ=0 EndX=580.085 EndY=-482.6 EndZ=0
    g276: Circle CenterX=634.695 CenterY=-482.6 CenterZ=0 NormalX=0 NormalY=0 NormalZ=1 AngleXU=0 Radius=3.175
    g277: LineSegment StartX=580.085 StartY=-482.6 StartZ=0 EndX=634.695 EndY=-482.6 EndZ=0
    g278: Circle CenterX=689.305 CenterY=-482.6 CenterZ=0 NormalX=0 NormalY=0 NormalZ=1 AngleXU=0 Radius=3.175
    g279: LineSegment StartX=634.695 StartY=-482.6 StartZ=0 EndX=689.305 EndY=-482.6 EndZ=0
    g280: Circle CenterX=743.915 CenterY=-482.6 CenterZ=0 NormalX=0 NormalY=0 NormalZ=1 AngleXU=0 Radius=3.175
    g281: LineSegment StartX=689.305 StartY=-482.6 StartZ=0 EndX=743.915 EndY=-482.6 EndZ=0
    g282: Circle CenterX=33.9852 CenterY=-533.4 CenterZ=0 NormalX=0 NormalY=0 NormalZ=1 AngleXU=0 Radius=3.175
    g283: LineSegment StartX=33.9852 StartY=-482.6 StartZ=0 EndX=33.9852 EndY=-533.4 EndZ=0
    g284: Circle CenterX=307.035 CenterY=-533.4 CenterZ=0 NormalX=0 NormalY=0 NormalZ=1 AngleXU=0 Radius=3.175
    g285: Circle CenterX=361.645 CenterY=-533.4 CenterZ=0 NormalX=0 NormalY=0 NormalZ=1 AngleXU=0 Radius=3.175
    g286: LineSegment StartX=307.035 StartY=-533.4 StartZ=0 EndX=361.645 EndY=-533.4 EndZ=0
    g287: Circle CenterX=416.255 CenterY=-533.4 CenterZ=0 NormalX=0 NormalY=0 NormalZ=1 AngleXU=0 Radius=3.175
    g288: LineSegment StartX=361.645 StartY=-533.4 StartZ=0 EndX=416.255 EndY=-533.4 EndZ=0
    g289: Circle CenterX=470.865 CenterY=-533.4 CenterZ=0 NormalX=0 NormalY=0 NormalZ=1 AngleXU=0 Radius=3.175
    g290: LineSegment StartX=416.255 StartY=-533.4 StartZ=0 EndX=470.865 EndY=-533.4 EndZ=0
    g291: Circle CenterX=525.475 CenterY=-533.4 CenterZ=0 NormalX=0 NormalY=0 NormalZ=1 AngleXU=0 Radius=3.175
    g292: LineSegment StartX=470.865 StartY=-533.4 StartZ=0 EndX=525.475 EndY=-533.4 EndZ=0
    g293: Circle CenterX=580.085 CenterY=-533.4 CenterZ=0 NormalX=0 NormalY=0 NormalZ=1 AngleXU=0 Radius=3.175
    g294: LineSegment StartX=525.475 StartY=-533.4 StartZ=0 EndX=580.085 EndY=-533.4 EndZ=0
    g295: Circle CenterX=634.695 CenterY=-533.4 CenterZ=0 NormalX=0 NormalY=0 NormalZ=1 AngleXU=0 Radius=3.175
    g296: LineSegment StartX=580.085 StartY=-533.4 StartZ=0 EndX=634.695 EndY=-533.4 EndZ=0
    g297: Circle CenterX=689.305 CenterY=-533.4 CenterZ=0 NormalX=0 NormalY=0 NormalZ=1 AngleXU=0 Radius=3.175
    g298: LineSegment StartX=634.695 StartY=-533.4 StartZ=0 EndX=689.305 EndY=-533.4 EndZ=0
    g299: Circle CenterX=743.915 CenterY=-533.4 CenterZ=0 NormalX=0 NormalY=0 NormalZ=1 AngleXU=0 Radius=3.175
    g300: LineSegment StartX=689.305 StartY=-533.4 StartZ=0 EndX=743.915 EndY=-533.4 EndZ=0
    g301: Circle CenterX=307.035 CenterY=-584.2 CenterZ=0 NormalX=0 NormalY=0 NormalZ=1 AngleXU=0 Radius=3.175
    g302: Circle CenterX=361.645 CenterY=-584.2 CenterZ=0 NormalX=0 NormalY=0 NormalZ=1 AngleXU=0 Radius=3.175
    g303: LineSegment StartX=307.035 StartY=-584.2 StartZ=0 EndX=361.645 EndY=-584.2 EndZ=0
    g304: Circle CenterX=416.255 CenterY=-584.2 CenterZ=0 NormalX=0 NormalY=0 NormalZ=1 AngleXU=0 Radius=3.175
    g305: LineSegment StartX=361.645 StartY=-584.2 StartZ=0 EndX=416.255 EndY=-584.2 EndZ=0
    g306: Circle CenterX=470.865 CenterY=-584.2 CenterZ=0 NormalX=0 NormalY=0 NormalZ=1 AngleXU=0 Radius=3.175
    g307: LineSegment StartX=416.255 StartY=-584.2 StartZ=0 EndX=470.865 EndY=-584.2 EndZ=0
    g308: Circle CenterX=525.475 CenterY=-584.2 CenterZ=0 NormalX=0 NormalY=0 NormalZ=1 AngleXU=0 Radius=3.175
    g309: LineSegment StartX=470.865 StartY=-584.2 StartZ=0 EndX=525.475 EndY=-584.2 EndZ=0
    g310: Circle CenterX=580.085 CenterY=-584.2 CenterZ=0 NormalX=0 NormalY=0 NormalZ=1 AngleXU=0 Radius=3.175
    g311: LineSegment StartX=525.475 StartY=-584.2 StartZ=0 EndX=580.085 EndY=-584.2 EndZ=0
    g312: Circle CenterX=634.695 CenterY=-584.2 CenterZ=0 NormalX=0 NormalY=0 NormalZ=1 AngleXU=0 Radius=3.175
    g313: LineSegment StartX=580.085 StartY=-584.2 StartZ=0 EndX=634.695 EndY=-584.2 EndZ=0
    g314: Circle CenterX=689.305 CenterY=-584.2 CenterZ=0 NormalX=0 NormalY=0 NormalZ=1 AngleXU=0 Radius=3.175
    g315: LineSegment StartX=634.695 StartY=-584.2 StartZ=0 EndX=689.305 EndY=-584.2 EndZ=0
    g316: Circle CenterX=743.915 CenterY=-584.2 CenterZ=0 NormalX=0 NormalY=0 NormalZ=1 AngleXU=0 Radius=3.175
    g317: LineSegment StartX=689.305 StartY=-584.2 StartZ=0 EndX=743.915 EndY=-584.2 EndZ=0
    g318: Circle CenterX=307.035 CenterY=-635 CenterZ=0 NormalX=0 NormalY=0 NormalZ=1 AngleXU=0 Radius=3.175
    g319: Circle CenterX=361.645 CenterY=-635 CenterZ=0 NormalX=0 NormalY=0 NormalZ=1 AngleXU=0 Radius=3.175
    g320: LineSegment StartX=307.035 StartY=-635 StartZ=0 EndX=361.645 EndY=-635 EndZ=0
    g321: Circle CenterX=416.255 CenterY=-635 CenterZ=0 NormalX=0 NormalY=0 NormalZ=1 AngleXU=0 Radius=3.175
    g322: LineSegment StartX=361.645 StartY=-635 StartZ=0 EndX=416.255 EndY=-635 EndZ=0
    g323: Circle CenterX=470.865 CenterY=-635 CenterZ=0 NormalX=0 NormalY=0 NormalZ=1 AngleXU=0 Radius=3.175
    g324: LineSegment StartX=416.255 StartY=-635 StartZ=0 EndX=470.865 EndY=-635 EndZ=0
    g325: Circle CenterX=525.475 CenterY=-635 CenterZ=0 NormalX=0 NormalY=0 NormalZ=1 AngleXU=0 Radius=3.175
    g326: LineSegment StartX=470.865 StartY=-635 StartZ=0 EndX=525.475 EndY=-635 EndZ=0
    g327: Circle CenterX=580.085 CenterY=-635 CenterZ=0 NormalX=0 NormalY=0 NormalZ=1 AngleXU=0 Radius=3.175
    g328: LineSegment StartX=525.475 StartY=-635 StartZ=0 EndX=580.085 EndY=-635 EndZ=0
    g329: Circle CenterX=634.695 CenterY=-635 CenterZ=0 NormalX=0 NormalY=0 NormalZ=1 AngleXU=0 Radius=3.175
    g330: LineSegment StartX=580.085 StartY=-635 StartZ=0 EndX=634.695 EndY=-635 EndZ=0
    g331: Circle CenterX=689.305 CenterY=-635 CenterZ=0 NormalX=0 NormalY=0 NormalZ=1 AngleXU=0 Radius=3.175
    g332: LineSegment StartX=634.695 StartY=-635 StartZ=0 EndX=689.305 EndY=-635 EndZ=0
    g333: Circle CenterX=743.915 CenterY=-635 CenterZ=0 NormalX=0 NormalY=0 NormalZ=1 AngleXU=0 Radius=3.175
    g334: LineSegment StartX=689.305 StartY=-635 StartZ=0 EndX=743.915 EndY=-635 EndZ=0
    g335: Circle CenterX=307.035 CenterY=-685.8 CenterZ=0 NormalX=0 NormalY=0 NormalZ=1 AngleXU=0 Radius=3.175
    g336: Circle CenterX=361.645 CenterY=-685.8 CenterZ=0 NormalX=0 NormalY=0 NormalZ=1 AngleXU=0 Radius=3.175
    g337: LineSegment StartX=307.035 StartY=-685.8 StartZ=0 EndX=361.645 EndY=-685.8 EndZ=0
    g338: Circle CenterX=416.255 CenterY=-685.8 CenterZ=0 NormalX=0 NormalY=0 NormalZ=1 AngleXU=0 Radius=3.175
    g339: LineSegment StartX=361.645 StartY=-685.8 StartZ=0 EndX=416.255 EndY=-685.8 EndZ=0
    g340: Circle CenterX=470.865 CenterY=-685.8 CenterZ=0 NormalX=0 NormalY=0 NormalZ=1 AngleXU=0 Radius=3.175
    g341: LineSegment StartX=416.255 StartY=-685.8 StartZ=0 EndX=470.865 EndY=-685.8 EndZ=0
    g342: Circle CenterX=525.475 CenterY=-685.8 CenterZ=0 NormalX=0 NormalY=0 NormalZ=1 AngleXU=0 Radius=3.175
    g343: LineSegment StartX=470.865 StartY=-685.8 StartZ=0 EndX=525.475 EndY=-685.8 EndZ=0
    g344: Circle CenterX=580.085 CenterY=-685.8 CenterZ=0 NormalX=0 NormalY=0 NormalZ=1 AngleXU=0 Radius=3.175
    g345: LineSegment StartX=525.475 StartY=-685.8 StartZ=0 EndX=580.085 EndY=-685.8 EndZ=0
    g346: Circle CenterX=634.695 CenterY=-685.8 CenterZ=0 NormalX=0 NormalY=0 NormalZ=1 AngleXU=0 Radius=3.175
    g347: LineSegment StartX=580.085 StartY=-685.8 StartZ=0 EndX=634.695 EndY=-685.8 EndZ=0
    g348: Circle CenterX=689.305 CenterY=-685.8 CenterZ=0 NormalX=0 NormalY=0 NormalZ=1 AngleXU=0 Radius=3.175
    g349: LineSegment StartX=634.695 StartY=-685.8 StartZ=0 EndX=689.305 EndY=-685.8 EndZ=0
    g350: Circle CenterX=743.915 CenterY=-685.8 CenterZ=0 NormalX=0 NormalY=0 NormalZ=1 AngleXU=0 Radius=3.175
    g351: LineSegment StartX=689.305 StartY=-685.8 StartZ=0 EndX=743.915 EndY=-685.8 EndZ=0
  constraints (877):
    c: Coincident(g0,g1)
    c: Coincident(g2,g0)
    c: Horizontal(g0)
    c: Vertical(g1)
    c: Vertical(g2)
    c: Distance(g0) = 777.875
    c: Distance(g2) = 711.2
    c: Coincident(g0,g-1)
    c: Vertical(g3)
    c: Vertical(g4)
    c: Coincident(g5,g2)
    c: Horizontal(g5)
    c: Coincident(g6,g1)
    c: Horizontal(g6)
    c: Distance(g5) = 66.675
    c: Coincident(g4,g5)
    c: Distance(g3) = 254
    c: Coincident(g6,g3)
    c: Equal(g2,g1)
    c: Equal(g3,g4)
    c: Distance(g4,g3) = 212.725
    c: Coincident(g7,g4)
    c: Horizontal(g7)
    c: Coincident(g8,g7)
    c: Vertical(g8)
    c: Coincident(g9,g8)
    c: Horizontal(g9)
    c: Coincident(g10,g9)
    c: Vertical(g10)
    c: Coincident(g11,g3)
    c: Coincident(g11,g10)
    c: Horizontal(g11)
    c: Distance(g9,g6) = 246.075
    c: Distance(g9) = 193.675
    c: Distance(g7) = 9.525
    c: Diameter(g12) = 6.35
    c: Distance(g12,g2) = 33.9852
    c: Distance(g12,g0) = 25.4
    c: Diameter(g13) = 6.35
    c: Coincident(g12,g14)
    c: Coincident(g13,g14)
    c: Distance(g14) = 54.61
    c: Angle(g14) = 0
    c: Diameter(g15) = 6.35
    c: Coincident(g13,g16)
    c: Coincident(g15,g16)
    c: Equal(g14,g16)
    c: Parallel(g16,g14)
    c: Diameter(g17) = 6.35
    c: Coincident(g15,g18)
    c: Coincident(g17,g18)
    c: Equal(g14,g18)
    c: Parallel(g18,g14)
    c: Diameter(g19) = 6.35
    c: Coincident(g17,g20)
    c: Coincident(g19,g20)
    c: Equal(g14,g20)
    c: Parallel(g20,g14)
    c: Diameter(g21) = 6.35
    c: Coincident(g19,g22)
    c: Coincident(g21,g22)
    c: Equal(g14,g22)
    c: Parallel(g22,g14)
    c: Diameter(g23) = 6.35
    c: Coincident(g21,g24)
    c: Coincident(g23,g24)
    c: Equal(g14,g24)
    c: Parallel(g24,g14)
    c: Diameter(g25) = 6.35
    c: Coincident(g23,g26)
    c: Coincident(g25,g26)
    c: Equal(g14,g26)
    c: Parallel(g26,g14)
    c: Diameter(g27) = 6.35
    c: Coincident(g25,g28)
    c: Coincident(g27,g28)
    c: Equal(g14,g28)
    c: Parallel(g28,g14)
    c: Diameter(g29) = 6.35
    c: Coincident(g27,g30)
    c: Coincident(g29,g30)
    c: Equal(g14,g30)
    c: Parallel(g30,g14)
    c: Diameter(g31) = 6.35
    c: Coincident(g29,g32)
    c: Coincident(g31,g32)
    c: Equal(g14,g32)
    c: Parallel(g32,g14)
    c: Diameter(g33) = 6.35
    c: Coincident(g31,g34)
    c: Coincident(g33,g34)
    c: Equal(g14,g34)
    c: Parallel(g34,g14)
    c: Diameter(g35) = 6.35
    c: Coincident(g33,g36)
    c: Coincident(g35,g36)
    c: Equal(g14,g36)
    c: Parallel(g36,g14)
    c: Diameter(g37) = 6.35
    c: Coincident(g35,g38)
    c: Coincident(g37,g38)
    c: Equal(g14,g38)
    c: Parallel(g38,g14)
    c: Diameter(g39) = 6.35
    c: Coincident(g12,g40)
    c: Coincident(g39,g40)
    c: Perpendicular(g40,g14)
    c: Diameter(g41) = 6.35
    c: Coincident(g39,g42)
    c: Coincident(g41,g42)
    c: Equal(g14,g42)
    c: Parallel(g42,g14)
    c: Diameter(g43) = 6.35
    c: Coincident(g41,g44)
    c: Coincident(g43,g44)
    c: Equal(g14,g44)
    c: Parallel(g44,g14)
    c: Diameter(g45) = 6.35
    c: Coincident(g43,g46)
    c: Coincident(g45,g46)
    c: Equal(g14,g46)
    c: Parallel(g46,g14)
    c: Diameter(g47) = 6.35
    c: Coincident(g45,g48)
    c: Coincident(g47,g48)
    c: Equal(g14,g48)
    c: Parallel(g48,g14)
    c: Diameter(g49) = 6.35
    c: Coincident(g47,g50)
    c: Coincident(g49,g50)
    c: Equal(g14,g50)
    c: Parallel(g50,g14)
    c: Diameter(g51) = 6.35
    c: Coincident(g49,g52)
    c: Coincident(g51,g52)
    c: Equal(g14,g52)
    c: Parallel(g52,g14)
    c: Diameter(g53) = 6.35
    c: Coincident(g51,g54)
    c: Coincident(g53,g54)
    c: Equal(g14,g54)
    c: Parallel(g54,g14)
    c: Diameter(g55) = 6.35
    c: Coincident(g53,g56)
    c: Coincident(g55,g56)
    c: Equal(g14,g56)
    c: Parallel(g56,g14)
    c: Diameter(g57) = 6.35
    c: Coincident(g55,g58)
    c: Coincident(g57,g58)
    c: Equal(g14,g58)
    c: Parallel(g58,g14)
    c: Diameter(g59) = 6.35
    c: Coincident(g57,g60)
    c: Coincident(g59,g60)
    c: Equal(g14,g60)
    c: Parallel(g60,g14)
    c: Diameter(g61) = 6.35
    c: Coincident(g59,g62)
    c: Coincident(g61,g62)
    c: Equal(g14,g62)
    c: Parallel(g62,g14)
    c: Diameter(g63) = 6.35
    c: Coincident(g61,g64)
    c: Coincident(g63,g64)
    c: Equal(g14,g64)
    c: Parallel(g64,g14)
    c: Diameter(g65) = 6.35
    c: Coincident(g63,g66)
    c: Coincident(g65,g66)
    c: Equal(g14,g66)
    c: Parallel(g66,g14)
    c: Diameter(g67) = 6.35
    c: Coincident(g39,g68)
    c: Coincident(g67,g68)
    c: Equal(g40,g68)
    c: Perpendicular(g68,g14)
    c: Diameter(g69) = 6.35
    c: Coincident(g67,g70)
    c: Coincident(g69,g70)
    c: Equal(g14,g70)
    c: Parallel(g70,g14)
    c: Diameter(g71) = 6.35
    c: Coincident(g69,g72)
    c: Coincident(g71,g72)
    c: Equal(g14,g72)
    c: Parallel(g72,g14)
    c: Diameter(g73) = 6.35
    c: Coincident(g71,g74)
    c: Coincident(g73,g74)
    c: Equal(g14,g74)
    c: Parallel(g74,g14)
    c: Diameter(g75) = 6.35
    c: Coincident(g73,g76)
    c: Coincident(g75,g76)
    c: Equal(g14,g76)
    c: Parallel(g76,g14)
    c: Diameter(g77) = 6.35
    c: Coincident(g75,g78)
    c: Coincident(g77,g78)
    c: Equal(g14,g78)
    c: Parallel(g78,g14)
    c: Diameter(g79) = 6.35
    c: Coincident(g77,g80)
    c: Coincident(g79,g80)
    c: Equal(g14,g80)
    c: Parallel(g80,g14)
    c: Diameter(g81) = 6.35
    c: Coincident(g79,g82)
    c: Coincident(g81,g82)
    c: Equal(g14,g82)
    c: Parallel(g82,g14)
    c: Diameter(g83) = 6.35
    c: Coincident(g81,g84)
    c: Coincident(g83,g84)
    c: Equal(g14,g84)
    c: Parallel(g84,g14)
    c: Diameter(g85) = 6.35
    c: Coincident(g83,g86)
    c: Coincident(g85,g86)
    c: Equal(g14,g86)
    c: Parallel(g86,g14)
    c: Diameter(g87) = 6.35
    c: Coincident(g85,g88)
    c: Coincident(g87,g88)
    c: Equal(g14,g88)
    c: Parallel(g88,g14)
    c: Diameter(g89) = 6.35
    c: Coincident(g87,g90)
    c: Coincident(g89,g90)
    c: Equal(g14,g90)
    c: Parallel(g90,g14)
    c: Diameter(g91) = 6.35
    c: Coincident(g89,g92)
    c: Coincident(g91,g92)
    c: Equal(g14,g92)
    c: Parallel(g92,g14)
    c: Diameter(g93) = 6.35
    c: Coincident(g91,g94)
    c: Coincident(g93,g94)
    c: Equal(g14,g94)
    c: Parallel(g94,g14)
    c: Diameter(g95) = 6.35
    c: Coincident(g67,g96)
    c: Coincident(g95,g96)
    c: Equal(g40,g96)
    c: Perpendicular(g96,g14)
    c: Diameter(g97) = 6.35
    c: Coincident(g95,g98)
    c: Coincident(g97,g98)
    c: Equal(g14,g98)
    c: Parallel(g98,g14)
    c: Diameter(g99) = 6.35
    c: Coincident(g97,g100)
    c: Coincident(g99,g100)
    c: Equal(g14,g100)
    c: Parallel(g100,g14)
    c: Diameter(g101) = 6.35
    c: Coincident(g99,g102)
    c: Coincident(g101,g102)
    c: Equal(g14,g102)
    c: Parallel(g102,g14)
    c: Diameter(g103) = 6.35
    c: Coincident(g101,g104)
    c: Coincident(g103,g104)
    c: Equal(g14,g104)
    c: Parallel(g104,g14)
    c: Diameter(g105) = 6.35
    c: Coincident(g103,g106)
    c: Coincident(g105,g106)
    c: Equal(g14,g106)
    c: Parallel(g106,g14)
    c: Diameter(g107) = 6.35
    c: Coincident(g105,g108)
    c: Coincident(g107,g108)
    c: Equal(g14,g108)
    c: Parallel(g108,g14)
    c: Diameter(g109) = 6.35
    c: Coincident(g107,g110)
    c: Coincident(g109,g110)
    c: Equal(g14,g110)
    c: Parallel(g110,g14)
    c: Diameter(g111) = 6.35
    c: Coincident(g109,g112)
    c: Coincident(g111,g112)
    c: Equal(g14,g112)
    c: Parallel(g112,g14)
    c: Diameter(g113) = 6.35
    c: Coincident(g111,g114)
    c: Coincident(g113,g114)
    c: Equal(g14,g114)
    c: Parallel(g114,g14)
    c: Diameter(g115) = 6.35
    c: Coincident(g113,g116)
    c: Coincident(g115,g116)
    c: Equal(g14,g116)
    c: Parallel(g116,g14)
    c: Diameter(g117) = 6.35
    c: Coincident(g115,g118)
    c: Coincident(g117,g118)
    c: Equal(g14,g118)
    c: Parallel(g118,g14)
    c: Diameter(g119) = 6.35
    c: Coincident(g117,g120)
    c: Coincident(g119,g120)
    c: Equal(g14,g120)
    c: Parallel(g120,g14)
    c: Diameter(g121) = 6.35
    c: Coincident(g119,g122)
    c: Coincident(g121,g122)
    c: Equal(g14,g122)
    c: Parallel(g122,g14)
    c: Diameter(g123) = 6.35
    c: Coincident(g95,g124)
    c: Coincident(g123,g124)
    c: Equal(g40,g124)
    c: Perpendicular(g124,g14)
    c: Diameter(g125) = 6.35
    c: Coincident(g123,g126)
    c: Coincident(g125,g126)
    c: Equal(g14,g126)
    c: Parallel(g126,g14)
    c: Diameter(g127) = 6.35
    c: Coincident(g125,g128)
    c: Coincident(g127,g128)
    c: Equal(g14,g128)
    c: Parallel(g128,g14)
    c: Diameter(g129) = 6.35
    c: Coincident(g127,g130)
    c: Coincident(g129,g130)
    c: Equal(g14,g130)
    c: Parallel(g130,g14)
    c: Diameter(g131) = 6.35
    c: Coincident(g129,g132)
    c: Coincident(g131,g132)
    c: Equal(g14,g132)
    c: Parallel(g132,g14)
    c: Diameter(g133) = 6.35
    c: Coincident(g131,g134)
    c: Coincident(g133,g134)
    c: Equal(g14,g134)
    c: Parallel(g134,g14)
    c: Diameter(g135) = 6.35
    c: Coincident(g133,g136)
    c: Coincident(g135,g136)
    c: Equal(g14,g136)
    c: Parallel(g136,g14)
    c: Diameter(g137) = 6.35
    c: Coincident(g135,g138)
    c: Coincident(g137,g138)
    c: Equal(g14,g138)
    c: Parallel(g138,g14)
    c: Diameter(g139) = 6.35
    c: Coincident(g137,g140)
    c: Coincident(g139,g140)
    c: Equal(g14,g140)
    c: Parallel(g140,g14)
    c: Diameter(g141) = 6.35
    c: Coincident(g139,g142)
    c: Coincident(g141,g142)
    c: Equal(g14,g142)
    c: Parallel(g142,g14)
    c: Diameter(g143) = 6.35
    c: Coincident(g141,g144)
    c: Coincident(g143,g144)
    c: Equal(g14,g144)
    c: Parallel(g144,g14)
    c: Diameter(g145) = 6.35
    c: Coincident(g143,g146)
    c: Coincident(g145,g146)
    c: Equal(g14,g146)
    c: Parallel(g146,g14)
    c: Diameter(g147) = 6.35
    c: Coincident(g145,g148)
    c: Coincident(g147,g148)
    c: Equal(g14,g148)
    c: Parallel(g148,g14)
    c: Diameter(g149) = 6.35
    c: Coincident(g147,g150)
    c: Coincident(g149,g150)
    c: Equal(g14,g150)
    c: Parallel(g150,g14)
    c: Diameter(g151) = 6.35
    c: Coincident(g123,g152)
    c: Coincident(g151,g152)
    c: Equal(g40,g152)
    c: Perpendicular(g152,g14)
    c: Diameter(g153) = 6.35
    c: Coincident(g151,g154)
    c: Coincident(g153,g154)
    c: Equal(g14,g154)
    c: Parallel(g154,g14)
    c: Diameter(g155) = 6.35
    c: Coincident(g153,g156)
    c: Coincident(g155,g156)
    c: Equal(g14,g156)
    c: Parallel(g156,g14)
    c: Diameter(g157) = 6.35
    c: Coincident(g155,g158)
    c: Coincident(g157,g158)
    c: Equal(g14,g158)
    c: Parallel(g158,g14)
    c: Diameter(g159) = 6.35
    c: Coincident(g157,g160)
    c: Coincident(g159,g160)
    c: Equal(g14,g160)
    c: Parallel(g160,g14)
    c: Diameter(g161) = 6.35
    c: Coincident(g159,g162)
    c: Coincident(g161,g162)
    c: Equal(g14,g162)
    c: Parallel(g162,g14)
    c: Diameter(g163) = 6.35
    c: Coincident(g161,g164)
    c: Coincident(g163,g164)
    c: Equal(g14,g164)
    c: Parallel(g164,g14)
    c: Diameter(g165) = 6.35
    c: Coincident(g163,g166)
    c: Coincident(g165,g166)
    c: Equal(g14,g166)
    c: Parallel(g166,g14)
    c: Diameter(g167) = 6.35
    c: Coincident(g165,g168)
    c: Coincident(g167,g168)
    c: Equal(g14,g168)
    c: Parallel(g168,g14)
    c: Diameter(g169) = 6.35
    c: Coincident(g167,g170)
    c: Coincident(g169,g170)
    c: Equal(g14,g170)
    c: Parallel(g170,g14)
    c: Diameter(g171) = 6.35
    c: Coincident(g169,g172)
    c: Coincident(g171,g172)
    c: Equal(g14,g172)
    c: Parallel(g172,g14)
    c: Diameter(g173) = 6.35
    c: Coincident(g171,g174)
    c: Coincident(g173,g174)
    c: Equal(g14,g174)
    c: Parallel(g174,g14)
    c: Diameter(g175) = 6.35
    c: Coincident(g173,g176)
    c: Coincident(g175,g176)
    c: Equal(g14,g176)
    c: Parallel(g176,g14)
    c: Diameter(g177) = 6.35
    c: Coincident(g175,g178)
    c: Coincident(g177,g178)
    c: Equal(g14,g178)
    c: Parallel(g178,g14)
    c: Diameter(g179) = 6.35
    c: Coincident(g151,g180)
    c: Coincident(g179,g180)
    c: Equal(g40,g180)
    c: Perpendicular(g180,g14)
    c: Diameter(g181) = 6.35
    c: Coincident(g179,g182)
    c: Coincident(g181,g182)
    c: Equal(g14,g182)
    c: Parallel(g182,g14)
    c: Diameter(g183) = 6.35
    c: Coincident(g181,g184)
    c: Coincident(g183,g184)
    c: Equal(g14,g184)
    c: Parallel(g184,g14)
    c: Diameter(g185) = 6.35
    c: Coincident(g183,g186)
    c: Coincident(g185,g186)
    c: Equal(g14,g186)
    c: Parallel(g186,g14)
    c: Diameter(g187) = 6.35
    c: Coincident(g185,g188)
    c: Coincident(g187,g188)
    c: Equal(g14,g188)
    c: Parallel(g188,g14)
    c: Diameter(g189) = 6.35
    c: Coincident(g187,g190)
    c: Coincident(g189,g190)
    c: Equal(g14,g190)
    c: Parallel(g190,g14)
    c: Diameter(g191) = 6.35
    c: Coincident(g189,g192)
    c: Coincident(g191,g192)
    c: Equal(g14,g192)
    c: Parallel(g192,g14)
    c: Diameter(g193) = 6.35
    c: Coincident(g191,g194)
    c: Coincident(g193,g194)
    c: Equal(g14,g194)
    c: Parallel(g194,g14)
    c: Diameter(g195) = 6.35
    c: Coincident(g193,g196)
    c: Coincident(g195,g196)
    c: Equal(g14,g196)
    c: Parallel(g196,g14)
    c: Diameter(g197) = 6.35
    c: Coincident(g195,g198)
    c: Coincident(g197,g198)
    c: Equal(g14,g198)
    c: Parallel(g198,g14)
    c: Diameter(g199) = 6.35
    c: Coincident(g197,g200)
    c: Coincident(g199,g200)
    c: Equal(g14,g200)
    c: Parallel(g200,g14)
    c: Diameter(g201) = 6.35
    c: Coincident(g199,g202)
    c: Coincident(g201,g202)
    c: Equal(g14,g202)
    c: Parallel(g202,g14)
    c: Diameter(g203) = 6.35
    c: Coincident(g201,g204)
    c: Coincident(g203,g204)
    c: Equal(g14,g204)
    c: Parallel(g204,g14)
    c: Diameter(g205) = 6.35
    c: Coincident(g203,g206)
    c: Coincident(g205,g206)
    c: Equal(g14,g206)
    c: Parallel(g206,g14)
    c: Diameter(g207) = 6.35
    c: Coincident(g179,g208)
    c: Coincident(g207,g208)
    c: Equal(g40,g208)
    c: Perpendicular(g208,g14)
    c: Diameter(g209) = 6.35
    c: Coincident(g207,g210)
    c: Coincident(g209,g210)
    c: Equal(g14,g210)
    c: Parallel(g210,g14)
    c: Diameter(g211) = 6.35
    c: Coincident(g209,g212)
    c: Coincident(g211,g212)
    c: Equal(g14,g212)
    c: Parallel(g212,g14)
    c: Diameter(g213) = 6.35
    c: Coincident(g211,g214)
    c: Coincident(g213,g214)
    c: Equal(g14,g214)
    c: Parallel(g214,g14)
    c: Diameter(g215) = 6.35
    c: Coincident(g213,g216)
    c: Coincident(g215,g216)
    c: Equal(g14,g216)
    c: Parallel(g216,g14)
    c: Diameter(g217) = 6.35
    c: Coincident(g215,g218)
    c: Coincident(g217,g218)
    c: Equal(g14,g218)
    c: Parallel(g218,g14)
    c: Diameter(g219) = 6.35
    c: Coincident(g217,g220)
    c: Coincident(g219,g220)
    c: Equal(g14,g220)
    c: Parallel(g220,g14)
    c: Diameter(g221) = 6.35
    c: Coincident(g219,g222)
    c: Coincident(g221,g222)
    c: Equal(g14,g222)
    c: Parallel(g222,g14)
    c: Diameter(g223) = 6.35
    c: Coincident(g221,g224)
    c: Coincident(g223,g224)
    c: Equal(g14,g224)
    c: Parallel(g224,g14)
    c: Diameter(g225) = 6.35
    c: Coincident(g223,g226)
    c: Coincident(g225,g226)
    c: Equal(g14,g226)
    c: Parallel(g226,g14)
    c: Diameter(g227) = 6.35
    c: Coincident(g225,g228)
    c: Coincident(g227,g228)
    c: Equal(g14,g228)
    c: Parallel(g228,g14)
    c: Diameter(g229) = 6.35
    c: Coincident(g227,g230)
    c: Coincident(g229,g230)
    c: Equal(g14,g230)
    c: Parallel(g230,g14)
    c: Diameter(g231) = 6.35
    c: Coincident(g229,g232)
    c: Coincident(g231,g232)
    c: Equal(g14,g232)
    c: Parallel(g232,g14)
    c: Diameter(g233) = 6.35
    c: Coincident(g231,g234)
    c: Coincident(g233,g234)
    c: Equal(g14,g234)
    c: Parallel(g234,g14)
    c: Diameter(g235) = 6.35
    c: Coincident(g207,g236)
    c: Coincident(g235,g236)
    c: Equal(g40,g236)
    c: Perpendicular(g236,g14)
    c: Diameter(g237) = 6.35
    c: Coincident(g235,g238)
    c: Coincident(g237,g238)
    c: Equal(g14,g238)
    c: Parallel(g238,g14)
    c: Diameter(g239) = 6.35
    c: Coincident(g237,g240)
    c: Coincident(g239,g240)
    c: Equal(g14,g240)
    c: Parallel(g240,g14)
    c: Diameter(g241) = 6.35
    c: Coincident(g239,g242)
    c: Coincident(g241,g242)
    c: Equal(g14,g242)
    c: Parallel(g242,g14)
    c: Diameter(g243) = 6.35
    c: Coincident(g241,g244)
    c: Coincident(g243,g244)
    c: Equal(g14,g244)
    c: Parallel(g244,g14)
    c: Diameter(g245) = 6.35
    c: Coincident(g243,g246)
    c: Coincident(g245,g246)
    c: Equal(g14,g246)
    c: Parallel(g246,g14)
    c: Diameter(g247) = 6.35
    c: Coincident(g245,g248)
    c: Coincident(g247,g248)
    c: Equal(g14,g248)
    c: Parallel(g248,g14)
    c: Diameter(g249) = 6.35
    c: Coincident(g247,g250)
    c: Coincident(g249,g250)
    c: Equal(g14,g250)
    c: Parallel(g250,g14)
    c: Diameter(g251) = 6.35
    c: Coincident(g249,g252)
    c: Coincident(g251,g252)
    c: Equal(g14,g252)
    c: Parallel(g252,g14)
    c: Diameter(g253) = 6.35
    c: Coincident(g251,g254)
    c: Coincident(g253,g254)
    c: Equal(g14,g254)
    c: Parallel(g254,g14)
    c: Diameter(g255) = 6.35
    c: Coincident(g253,g256)
    c: Coincident(g255,g256)
    c: Equal(g14,g256)
    c: Parallel(g256,g14)
    c: Diameter(g257) = 6.35
    c: Coincident(g255,g258)
    c: Coincident(g257,g258)
    c: Equal(g14,g258)
    c: Parallel(g258,g14)
    c: Diameter(g259) = 6.35
    c: Coincident(g257,g260)
    c: Coincident(g259,g260)
    c: Equal(g14,g260)
    c: Parallel(g260,g14)
    c: Diameter(g261) = 6.35
    c: Coincident(g259,g262)
    c: Coincident(g261,g262)
    c: Equal(g14,g262)
    c: Parallel(g262,g14)
    c: Diameter(g263) = 6.35
    c: Coincident(g235,g264)
    c: Coincident(g263,g264)
    c: Equal(g40,g264)
    c: Perpendicular(g264,g14)
    c: Diameter(g265) = 6.35
    c: Diameter(g266) = 6.35
    c: Coincident(g265,g267)
    c: Coincident(g266,g267)
    c: Equal(g14,g267)
    c: Parallel(g267,g14)
    c: Diameter(g268) = 6.35
    c: Coincident(g266,g269)
    c: Coincident(g268,g269)
    c: Equal(g14,g269)
    c: Parallel(g269,g14)
    c: Diameter(g270) = 6.35
    c: Coincident(g268,g271)
    c: Coincident(g270,g271)
    c: Equal(g14,g271)
    c: Parallel(g271,g14)
    c: Diameter(g272) = 6.35
    c: Coincident(g270,g273)
    c: Coincident(g272,g273)
    c: Equal(g14,g273)
    c: Parallel(g273,g14)
    c: Diameter(g274) = 6.35
    c: Coincident(g272,g275)
    c: Coincident(g274,g275)
    c: Equal(g14,g275)
    c: Parallel(g275,g14)
    c: Diameter(g276) = 6.35
    c: Coincident(g274,g277)
    c: Coincident(g276,g277)
    c: Equal(g14,g277)
    c: Parallel(g277,g14)
    c: Diameter(g278) = 6.35
    c: Coincident(g276,g279)
    c: Coincident(g278,g279)
    c: Equal(g14,g279)
    c: Parallel(g279,g14)
    c: Diameter(g280) = 6.35
    c: Coincident(g278,g281)
    c: Coincident(g280,g281)
    c: Equal(g14,g281)
    c: Parallel(g281,g14)
    c: Diameter(g282) = 6.35
    c: Coincident(g263,g283)
    c: Coincident(g282,g283)
    c: Equal(g40,g283)
    c: Perpendicular(g283,g14)
    c: Diameter(g284) = 6.35
    c: Diameter(g285) = 6.35
    c: Coincident(g284,g286)
    c: Coincident(g285,g286)
    c: Equal(g14,g286)
    c: Parallel(g286,g14)
    c: Diameter(g287) = 6.35
    c: Coincident(g285,g288)
    c: Coincident(g287,g288)
    c: Equal(g14,g288)
    c: Parallel(g288,g14)
    c: Diameter(g289) = 6.35
    c: Coincident(g287,g290)
    c: Coincident(g289,g290)
    c: Equal(g14,g290)
    c: Parallel(g290,g14)
    c: Diameter(g291) = 6.35
    c: Coincident(g289,g292)
    c: Coincident(g291,g292)
    c: Equal(g14,g292)
    c: Parallel(g292,g14)
    c: Diameter(g293) = 6.35
    c: Coincident(g291,g294)
    c: Coincident(g293,g294)
    c: Equal(g14,g294)
    c: Parallel(g294,g14)
    c: Diameter(g295) = 6.35
    c: Coincident(g293,g296)
    c: Coincident(g295,g296)
    c: Equal(g14,g296)
    c: Parallel(g296,g14)
    c: Diameter(g297) = 6.35
    c: Coincident(g295,g298)
    c: Coincident(g297,g298)
    c: Equal(g14,g298)
    c: Parallel(g298,g14)
    c: Diameter(g299) = 6.35
    c: Coincident(g297,g300)
    c: Coincident(g299,g300)
    c: Equal(g14,g300)
    c: Parallel(g300,g14)
    c: Diameter(g301) = 6.35
    c: Diameter(g302) = 6.35
    c: Coincident(g301,g303)
    c: Coincident(g302,g303)
    c: Equal(g14,g303)
    c: Parallel(g303,g14)
    c: Diameter(g304) = 6.35
    c: Coincident(g302,g305)
    c: Coincident(g304,g305)
    c: Equal(g14,g305)
    c: Parallel(g305,g14)
    c: Diameter(g306) = 6.35
    c: Coincident(g304,g307)
    c: Coincident(g306,g307)
    c: Equal(g14,g307)
    c: Parallel(g307,g14)
    c: Diameter(g308) = 6.35
    c: Coincident(g306,g309)
    c: Coincident(g308,g309)
    c: Equal(g14,g309)
    c: Parallel(g309,g14)
    c: Diameter(g310) = 6.35
    c: Coincident(g308,g311)
    c: Coincident(g310,g311)
    c: Equal(g14,g311)
    c: Parallel(g311,g14)
    c: Diameter(g312) = 6.35
    c: Coincident(g310,g313)
    c: Coincident(g312,g313)
    c: Equal(g14,g313)
    c: Parallel(g313,g14)
    c: Diameter(g314) = 6.35
    c: Coincident(g312,g315)
    c: Coincident(g314,g315)
    c: Equal(g14,g315)
    c: Parallel(g315,g14)
    c: Diameter(g316) = 6.35
    c: Coincident(g314,g317)
    c: Coincident(g316,g317)
    c: Equal(g14,g317)
    c: Parallel(g317,g14)
    c: Diameter(g318) = 6.35
    c: Diameter(g319) = 6.35
    c: Coincident(g318,g320)
    c: Coincident(g319,g320)
    c: Equal(g14,g320)
    c: Parallel(g320,g14)
    c: Diameter(g321) = 6.35
    c: Coincident(g319,g322)
    c: Coincident(g321,g322)
    c: Equal(g14,g322)
    c: Parallel(g322,g14)
    c: Diameter(g323) = 6.35
    c: Coincident(g321,g324)
    c: Coincident(g323,g324)
    c: Equal(g14,g324)
    c: Parallel(g324,g14)
    c: Diameter(g325) = 6.35
    c: Coincident(g323,g326)
    c: Coincident(g325,g326)
    c: Equal(g14,g326)
    c: Parallel(g326,g14)
    c: Diameter(g327) = 6.35
    c: Coincident(g325,g328)
    c: Coincident(g327,g328)
    c: Equal(g14,g328)
    c: Parallel(g328,g14)
    c: Diameter(g329) = 6.35
    c: Coincident(g327,g330)
    c: Coincident(g329,g330)
    c: Equal(g14,g330)
    c: Parallel(g330,g14)
    c: Diameter(g331) = 6.35
    c: Coincident(g329,g332)
    c: Coincident(g331,g332)
    c: Equal(g14,g332)
    c: Parallel(g332,g14)
    c: Diameter(g333) = 6.35
    c: Coincident(g331,g334)
    c: Coincident(g333,g334)
    c: Equal(g14,g334)
    c: Parallel(g334,g14)
    c: Diameter(g335) = 6.35
    c: Diameter(g336) = 6.35
    c: Coincident(g335,g337)
    c: Coincident(g336,g337)
    c: Equal(g14,g337)
    c: Parallel(g337,g14)
    c: Diameter(g338) = 6.35
    c: Coincident(g336,g339)
    c: Coincident(g338,g339)
    c: Equal(g14,g339)
    c: Parallel(g339,g14)
    c: Diameter(g340) = 6.35
    c: Coincident(g338,g341)
    c: Coincident(g340,g341)
    c: Equal(g14,g341)
    c: Parallel(g341,g14)
    c: Diameter(g342) = 6.35
    c: Coincident(g340,g343)
    c: Coincident(g342,g343)
    c: Equal(g14,g343)
    c: Parallel(g343,g14)
    c: Diameter(g344) = 6.35
    c: Coincident(g342,g345)
    c: Coincident(g344,g345)
    c: Equal(g14,g345)
    c: Parallel(g345,g14)
    c: Diameter(g346) = 6.35
    c: Coincident(g344,g347)
    c: Coincident(g346,g347)
    c: Equal(g14,g347)
    c: Parallel(g347,g14)
    c: Diameter(g348) = 6.35
    c: Coincident(g346,g349)
    c: Coincident(g348,g349)
    c: Equal(g14,g349)
    c: Parallel(g349,g14)
    c: Diameter(g350) = 6.35
    c: Coincident(g348,g351)
    c: Coincident(g350,g351)
    c: Equal(g14,g351)
    c: Parallel(g351,g14)
FEATURE [Part::Extrusion] Extrude
  Base = -> Sketch
  Dir = (0,0,1)
  DirMode = 2
  FaceMakerClass = Part::FaceMakerBullseye
  LengthFwd = 5.9944
  LengthRev = 0
  Solid = true
  Symmetric = false
FEATURE [TechDraw::DrawSVGTemplate] Template
  Height = 215.9
  Orientation = 1
  Width = 279.4
FEATURE [TechDraw::DrawProjGroupItem] ProjItem  label="Front"
  CoarseView = false
  Direction = (0,0,1)
  Focus = 100
  HardHidden = false
  IsoCount = 0
  IsoHidden = false
  IsoVisible = false
  LockPosition = true
  Perspective = false
  Rotation = 0
  RotationVector = (-1,0,0)
  Scale = 0.2
  ScaleType = 2
  SeamHidden = false
  SeamVisible = true
  SmoothHidden = false
  SmoothVisible = true
  Source = -> [Extrude]
  Type = 0
  X = 0
  XDirection = (1,1e-16,0)
  Y = 0
FEATURE [TechDraw::DrawProjGroupItem] ProjItem001  label="Left"
  CoarseView = false
  Direction = (-1,-1e-16,1e-16)
  Focus = 100
  HardHidden = false
  IsoCount = 0
  IsoHidden = false
  IsoVisible = false
  LockPosition = false
  Perspective = false
  Rotation = 0
  RotationVector = (1,0,0)
  ScaleType = 2
  SeamHidden = false
  SeamVisible = true
  SmoothHidden = false
  SmoothVisible = true
  Source = -> [Extrude]
  Type = 1
  X = 114.629
  XDirection = (1e-16,0,1)
  Y = 0
FEATURE [TechDraw::DrawProjGroup] ProjGroup
  Anchor = -> ProjItem
  AutoDistribute = true
  LockPosition = false
  ProjectionType = 0
  Rotation = 0
  Scale = 0.2
  ScaleType = 2
  Source = -> [Extrude]
  Views = -> [ProjItem,ProjItem001]
  X = 122.875
  Y = 96.5275
  spacingX = 15.0114
  spacingY = 15.0114
FEATURE [TechDraw::DrawHatch] Hatch  label="HatchF0"
  HatchPattern = <path>
  Source = -> ProjItem [Face0]
FEATURE [TechDraw::DrawHatch] Hatch001  label="Hatch001F0"
  HatchPattern = <path>
  Source = -> ProjItem001 [Face0]
FEATURE [TechDraw::DrawViewDimension] Dimension
  Arbitrary = false
  ArbitraryTolerances = false
  EqualTolerance = true
  FormatSpec = %.3f
  FormatSpecOverTolerance = %+.3f
  FormatSpecUnderTolerance = %+.3f
  Inverted = false
  LockPosition = false
  MeasureType = 1
  OverTolerance = 0
  References2D = -> [ProjItem001]
  Rotation = 0
  ScaleType = 0
  TheoreticalExact = false
  Type = 1
  UnderTolerance = 0
  X = 18.6629
  Y = 60.817
FEATURE [TechDraw::DrawViewDimension] Dimension001
  Arbitrary = false
  ArbitraryTolerances = false
  EqualTolerance = true
  FormatSpec = %.3f
  FormatSpecOverTolerance = %+.3f
  FormatSpecUnderTolerance = %+.3f
  Inverted = false
  LockPosition = false
  MeasureType = 1
  OverTolerance = 0
  References2D = -> [ProjItem]
  Rotation = 0
  ScaleType = 0
  TheoreticalExact = false
  Type = 2
  UnderTolerance = 0
  X = 91.8355
  Y = -0.510837
FEATURE [TechDraw::DrawViewDimension] Dimension002
  Arbitrary = false
  ArbitraryTolerances = false
  EqualTolerance = true
  FormatSpec = %.3f
  FormatSpecOverTolerance = %+.3f
  FormatSpecUnderTolerance = %+.3f
  Inverted = false
  LockPosition = false
  MeasureType = 1
  OverTolerance = 0
  References2D = -> [ProjItem]
  Rotation = 0
  ScaleType = 0
  TheoreticalExact = false
  Type = 1
  UnderTolerance = 0
  X = -0.177374
  Y = 97.3713
FEATURE [TechDraw::DrawViewDimension] Dimension003
  Arbitrary = false
  ArbitraryTolerances = false
  EqualTolerance = true
  FormatSpec = %.3f
  FormatSpecOverTolerance = %+.3f
  FormatSpecUnderTolerance = %+.3f
  Inverted = false
  LockPosition = false
  MeasureType = 1
  OverTolerance = 0
  References2D = -> [ProjItem]
  Rotation = 0
  ScaleType = 0
  TheoreticalExact = false
  Type = 1
  UnderTolerance = 0
  X = -95.3027
  Y = 64.7593
FEATURE [TechDraw::DrawViewDimension] Dimension004
  Arbitrary = false
  ArbitraryTolerances = false
  EqualTolerance = true
  FormatSpec = %.3f
  FormatSpecOverTolerance = %+.3f
  FormatSpecUnderTolerance = %+.3f
  Inverted = false
  LockPosition = false
  MeasureType = 1
  OverTolerance = 0
  References2D = -> [ProjItem]
  Rotation = 0
  ScaleType = 0
  TheoreticalExact = false
  Type = 2
  UnderTolerance = 0
  X = -65.8477
  Y = 85.2259
FEATURE [TechDraw::DrawViewDimension] Dimension005
  Arbitrary = false
  ArbitraryTolerances = false
  EqualTolerance = true
  FormatSpec = %.3f
  FormatSpecOverTolerance = %+.3f
  FormatSpecUnderTolerance = %+.3f
  Inverted = false
  LockPosition = false
  MeasureType = 1
  OverTolerance = 0
  References2D = -> [ProjItem]
  Rotation = 0
  ScaleType = 0
  TheoreticalExact = false
  Type = 1
  UnderTolerance = 0
  X = -94.591
  Y = 44.6666
FEATURE [TechDraw::DrawViewDimension] Dimension006
  Arbitrary = false
  ArbitraryTolerances = false
  EqualTolerance = true
  FormatSpec = %.3f
  FormatSpecOverTolerance = %+.3f
  FormatSpecUnderTolerance = %+.3f
  Inverted = false
  LockPosition = false
  MeasureType = 1
  OverTolerance = 0
  References2D = -> [ProjItem]
  Rotation = 0
  ScaleType = 0
  TheoreticalExact = false
  Type = 2
  UnderTolerance = 0
  X = -46.4753
  Y = 84.2277
FEATURE [TechDraw::DrawViewDimension] Dimension007
  Arbitrary = false
  ArbitraryTolerances = false
  EqualTolerance = true
  FormatSpec = ⌀%.3f
  FormatSpecOverTolerance = %+.3f
  FormatSpecUnderTolerance = %+.3f
  Inverted = false
  LockPosition = false
  MeasureType = 1
  OverTolerance = 0
  References2D = -> [ProjItem]
  Rotation = 0
  ScaleType = 0
  TheoreticalExact = false
  Type = 5
  UnderTolerance = 0
  X = -89.5084
  Y = 86.3306
FEATURE [TechDraw::DrawViewDimension] Dimension008
  Arbitrary = false
  ArbitraryTolerances = false
  EqualTolerance = true
  FormatSpec = %.3f
  FormatSpecOverTolerance = %+.3f
  FormatSpecUnderTolerance = %+.3f
  Inverted = false
  LockPosition = false
  MeasureType = 1
  OverTolerance = 0
  References2D = -> [ProjItem]
  Rotation = 0
  ScaleType = 0
  TheoreticalExact = false
  Type = 1
  UnderTolerance = 0
  X = -89.734
  Y = -78.7681
FEATURE [TechDraw::DrawViewDimension] Dimension009
  Arbitrary = false
  ArbitraryTolerances = false
  EqualTolerance = true
  FormatSpec = %.3f
  FormatSpecOverTolerance = %+.3f
  FormatSpecUnderTolerance = %+.3f
  Inverted = false
  LockPosition = false
  MeasureType = 1
  OverTolerance = 0
  References2D = -> [ProjItem]
  Rotation = 0
  ScaleType = 0
  TheoreticalExact = false
  Type = 1
  UnderTolerance = 0
  X = -42.6692
  Y = -78.7826
FEATURE [TechDraw::DrawViewDimension] Dimension010
  Arbitrary = false
  ArbitraryTolerances = false
  EqualTolerance = true
  FormatSpec = %.3f
  FormatSpecOverTolerance = %+.3f
  FormatSpecUnderTolerance = %+.3f
  Inverted = false
  LockPosition = false
  MeasureType = 1
  OverTolerance = 0
  References2D = -> [ProjItem]
  Rotation = 0
  ScaleType = 0
  TheoreticalExact = false
  Type = 1
  UnderTolerance = 0
  X = -51.3535
  Y = -33.1509
FEATURE [TechDraw::DrawViewDimension] Dimension011
  Arbitrary = false
  ArbitraryTolerances = false
  EqualTolerance = true
  FormatSpec = %.3f
  FormatSpecOverTolerance = %+.3f
  FormatSpecUnderTolerance = %+.3f
  Inverted = false
  LockPosition = false
  MeasureType = 1
  OverTolerance = 0
  References2D = -> [ProjItem]
  Rotation = 0
  ScaleType = 0
  TheoreticalExact = false
  Type = 1
  UnderTolerance = 0
  X = -33.3385
  Y = -33.0796
FEATURE [TechDraw::DrawViewDimension] Dimension012
  Arbitrary = false
  ArbitraryTolerances = false
  EqualTolerance = true
  FormatSpec = %.3f
  FormatSpecOverTolerance = %+.3f
  FormatSpecUnderTolerance = %+.3f
  Inverted = false
  LockPosition = false
  MeasureType = 1
  OverTolerance = 0
  References2D = -> [ProjItem]
  Rotation = 0
  ScaleType = 0
  TheoreticalExact = false
  Type = 2
  UnderTolerance = 0
  X = -55.8375
  Y = -7.45598
FEATURE [TechDraw::DrawViewDimension] Dimension013
  Arbitrary = false
  ArbitraryTolerances = false
  EqualTolerance = true
  FormatSpec = %.3f
  FormatSpecOverTolerance = %+.3f
  FormatSpecUnderTolerance = %+.3f
  Inverted = false
  LockPosition = false
  MeasureType = 1
  OverTolerance = 0
  References2D = -> [ProjItem]
  Rotation = 0
  ScaleType = 0
  TheoreticalExact = false
  Type = 2
  UnderTolerance = 0
  X = -33.4784
  Y = -7.59731
FEATURE [TechDraw::DrawViewDimension] Dimension015
  Arbitrary = false
  ArbitraryTolerances = false
  EqualTolerance = true
  FormatSpec = %.3f
  FormatSpecOverTolerance = %+.3f
  FormatSpecUnderTolerance = %+.3f
  Inverted = false
  LockPosition = false
  MeasureType = 1
  OverTolerance = 0
  References2D = -> [ProjItem]
  Rotation = 0
  ScaleType = 0
  TheoreticalExact = false
  Type = 2
  UnderTolerance = 0
  X = -10.6265
  Y = -44.0172
FEATURE [TechDraw::DrawViewAnnotation] Annotation
  Font = osifont
  LineSpace = 80
  LockPosition = false
  MaxWidth = -1
  Rotation = 0
  ScaleType = 0
  Text = Figure S1 (Inverted 1) | Panel 8 [right side interior baffle] | Quantity: 1
  TextSize = 5.0038
  TextStyle = 0
  X = 46.5241
  Y = 195.58
FEATURE [TechDraw::DrawViewAnnotation] Annotation002
  Font = osifont
  LineSpace = 80
  LockPosition = false
  MaxWidth = -1
  Rotation = 0
  ScaleType = 0
  Text = Units: Inches
  TextSize = 5.0038
  TextStyle = 0
  X = 259.08
  Y = 5.08
FEATURE [TechDraw::DrawViewAnnotation] Annotation003
  Font = osifont
  LineSpace = 80
  LockPosition = false
  MaxWidth = -1
  Rotation = 0
  ScaleType = 0
  Text = Repeat with equal spacing
  TextSize = 5.0038
  TextStyle = 0
  X = 117.54
  Y = 161.537
FEATURE [TechDraw::DrawPage] Page
  KeepUpdated = true
  NextBalloonIndex = 1
  ProjectionType = 0
  Template = -> Template
  Views = -> [ProjGroup,Dimension,Dimension001,Dimension002,Dimension003,Dimension004,Dimension005,Dimension006,Dimension007,Dimension008,Dimension009,Dimension010,Dimension011,Dimension012,Dimension013,Dimension015,Annotation,Annotation002,Annotation003]
note: 2 file-system paths scrubbed to <path> (originals preserved in the JSON sidecar)
